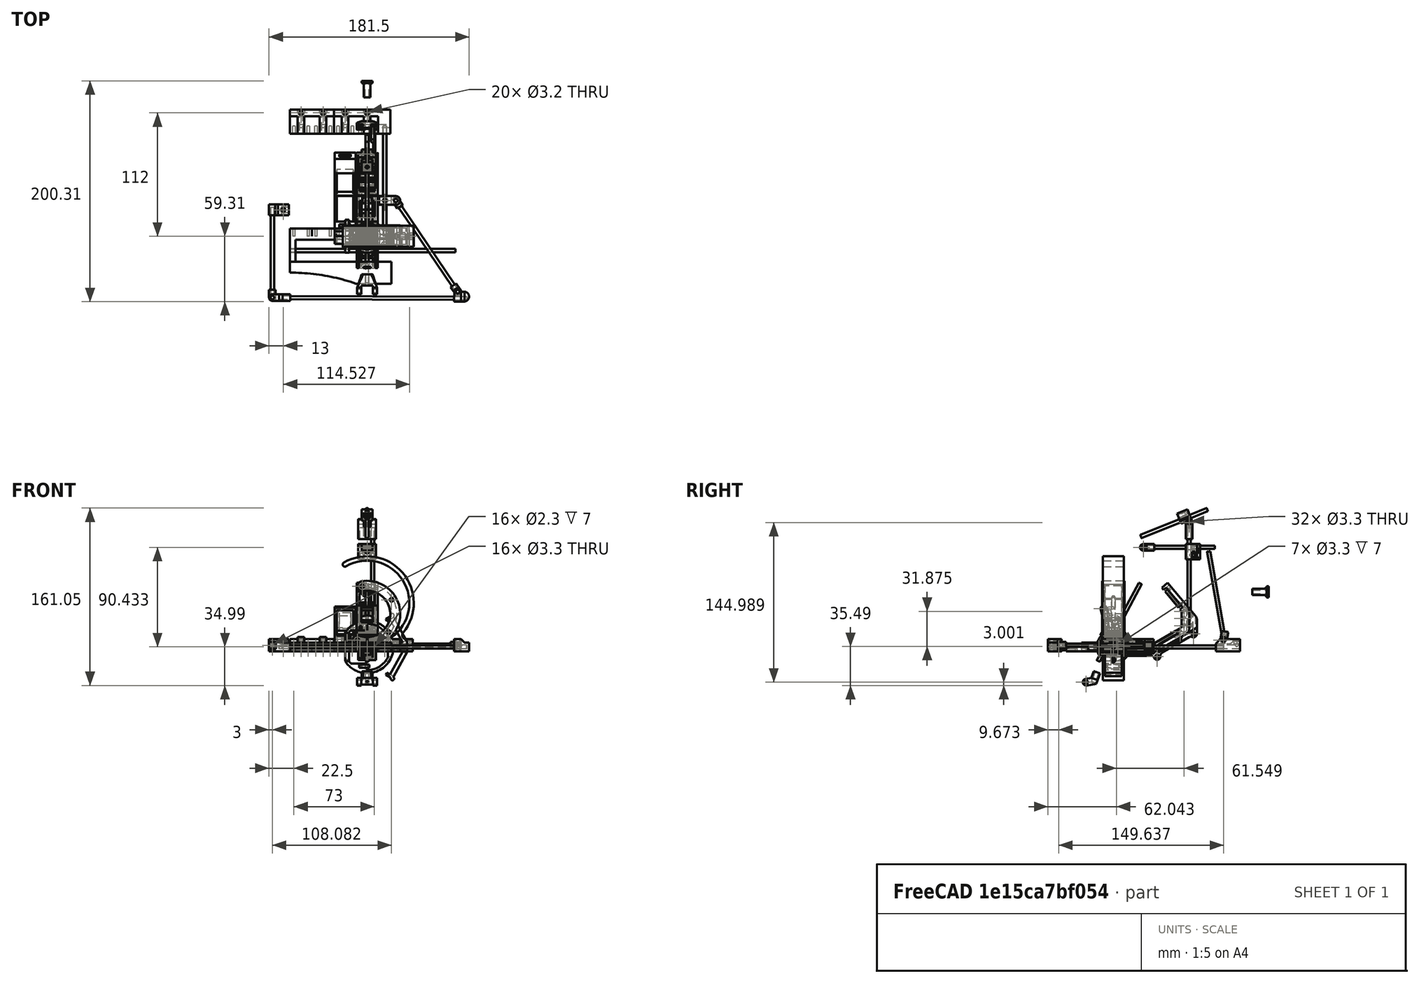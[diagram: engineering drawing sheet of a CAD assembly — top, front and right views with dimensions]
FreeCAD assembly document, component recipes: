
FREECAD ASSEMBLY — COMPONENT RECIPES ("Structure")

This assembly document has 6 components, labeled P0..P5 below (a component is one placed body or linked part). 4 of them carry a construction recipe — the FreeCAD feature program that regenerates the part from scratch, quoted from this document or its linked companion documents; the rest are supplied as boundary geometry only. No exploded tour is included for this assembly.
COMPONENT P0 — recipe-attached ("Base", modeled in this document).
Construction recipe (the document's own serialized feature program — sketch geometry with constraints, then the solid features built on it; lengths are millimeters unless a unit is written):

FEATURE [Sketcher::SketchObject] Sketch263  label="BaseSkeleton_KeyHolder"
  FullyConstrained = false
  MapMode = 5
  Placement = pos=(0,0,0) rot=(0.57735,0.57735,0.57735;2.0944rad)
  Support = -> [YZ_Plane106]
  expr: .Constraints.y0 = <<BaseParameters>>.horizontalRailLength
  expr: .Constraints.z0 = 6 + <<BaseParameters>>.tolerance
  expr: Constraints[13] = Sketch232.Constraints.l1
  expr: Constraints[14] = Sketch232.Constraints.l2
  expr: Constraints[15] = Sketch232.Constraints.l3
  expr: Constraints[16] = Sketch232.Constraints.theta1
  expr: Constraints[17] = Sketch232.Constraints.theta0
  expr: Constraints[27] = Sketch232.Constraints.theta2
  expr: Constraints[36] = <<BaseParameters>>.support0Length
  expr: Constraints[41] = 6 + 2 * <<BaseParameters>>.axisTolerance + <<BaseParameters>>.verticalRailLength
  expr: Constraints[57] = 1.5 + <<BaseParameters>>.axisTolerance
  expr: Constraints[60] = Sketch292.Constraints.y0
  expr: Constraints[69] = Sketch297.Constraints.theta0
  expr: Constraints[70] = Sketch297.Constraints.l0
  expr: Constraints[74] = Sketch203.Constraints.theta0
  expr: Constraints[89] = Sketch284.Constraints.l0 + <<BaseParameters>>.support1Length * 1mm
  sketch-geometry (28):
    g0: LineSegment StartX=0 StartY=0 StartZ=0 EndX=100 EndY=0 EndZ=0
    g1: LineSegment StartX=100 StartY=0 StartZ=0 EndX=100 EndY=6.15 EndZ=0
    g2: LineSegment StartX=100 StartY=6.15 StartZ=0 EndX=102.335 EndY=92.4184 EndZ=0
    g3: LineSegment StartX=100 StartY=6.15 StartZ=0 EndX=100 EndY=26.15 EndZ=0
    g4: LineSegment StartX=26.1808 StartY=28.1109 StartZ=0 EndX=63.4391 EndY=47.1897 EndZ=0
    g5: LineSegment StartX=63.4391 StartY=47.1897 StartZ=0 EndX=81.9391 EndY=81.3515 EndZ=0
    g6: LineSegment StartX=26.1808 StartY=28.1109 StartZ=0 EndX=24.669 EndY=34.9227 EndZ=0
    g7: GeomPoint X=-500 Y=0 Z=0
    g8: LineSegment StartX=24.669 StartY=34.9227 StartZ=0 EndX=24.669 EndY=54.9227 EndZ=0
    g9: LineSegment StartX=24.669 StartY=34.9227 StartZ=0 EndX=14.7136 EndY=52.2688 EndZ=0
    g10: GeomPoint X=46.4566 Y=0 Z=0
    g11: LineSegment StartX=46.4566 StartY=0 StartZ=0 EndX=46.4566 EndY=6 EndZ=0
    g12: LineSegment StartX=26.1808 StartY=28.1109 StartZ=0 EndX=46.4566 EndY=6 EndZ=0
    g13: LineSegment StartX=46.4566 StartY=6 StartZ=0 EndX=46.4566 EndY=26 EndZ=0
    g14: GeomPoint X=100.045 Y=7.7994 Z=0
    g15: GeomPoint X=101.083 Y=46.1708 Z=0
    g16: LineSegment StartX=63.4391 StartY=47.1897 StartZ=0 EndX=150.407 EndY=44.8358 EndZ=0
    g17: LineSegment StartX=63.4391 StartY=47.1897 StartZ=0 EndX=63.4391 EndY=67.1897 EndZ=0
    g18: LineSegment StartX=102.335 StartY=92.4184 StartZ=0 EndX=102.876 EndY=112.411 EndZ=0
    g19: LineSegment StartX=102.335 StartY=92.4184 StartZ=0 EndX=133.365 EndY=146.164 EndZ=0
    g20: LineSegment StartX=102.335 StartY=92.4184 StartZ=0 EndX=97.1388 EndY=95.4184 EndZ=0
    g21: LineSegment StartX=81.9391 StartY=81.3515 StartZ=0 EndX=102.021 EndY=80.808 EndZ=0
    g22: LineSegment StartX=81.9391 StartY=81.3515 StartZ=0 EndX=88.2853 EndY=80.0836 EndZ=0
    g23: LineSegment StartX=88.2853 StartY=80.0836 StartZ=0 EndX=126.04 EndY=145.477 EndZ=0
    g24: LineSegment StartX=81.9391 StartY=81.3515 StartZ=0 EndX=89.0173 EndY=81.3515 EndZ=0
    g25: LineSegment StartX=81.9391 StartY=81.3515 StartZ=0 EndX=82.4803 EndY=101.344 EndZ=0
    g26: LineSegment StartX=81.9391 StartY=81.3515 StartZ=0 EndX=81.9391 EndY=101.352 EndZ=0
    g27: LineSegment StartX=88.2853 StartY=80.0836 StartZ=0 EndX=101.991 EndY=79.7126 EndZ=0
  constraints (96):
    c: Coincident(g0,g-1)
    c: PointOnObject(g0,g-1)
    c: Distance(g0) = 100  'y0'
    c: Coincident(g0,g1)
    c: Vertical(g1)
    c: Distance(g1) = 6.15  'z0'
    c: Coincident(g2,g1)
    c: Coincident(g3,g1)
    c: Vertical(g3)
    c: Distance(g3) = 20
    c: Angle(g2,g3) = 0.0270601  'theta0'
    c: Coincident(g4,g5)
    c: Coincident(g6,g4)
    c: Distance(g6) = 6.97753
    c: Distance(g4) = 41.8591
    c: Distance(g5) = 38.8495
    c: Angle(g5,g4) = 2.54038
    c: Angle(g4,g6) = 1.31593
    c: PointOnObject(g7,g-1)
    c: Distance(g7,g-2) = 500  'yNeg'
    c: DistanceX(g7,g6) = 524.669  'y1'
    c: Distance(g6,g-1) = 34.9227  'z1'
    c: Coincident(g8,g6)
    c: Vertical(g8)
    c: Equal(g8,g3)
    c: Coincident(g9,g6)
    c: Equal(g9,g8)
    c: Angle(g9,g6) = 2.83896
    c: Angle(g8,g9) = 0.521027  'theta1'
    c: PointOnObject(g10,g0)
    c: Distance(g10,g-2) = 46.4566  'y2'
    c: Coincident(g11,g10)
    c: Vertical(g11)
    c: Distance(g11) = 6
    c: Coincident(g12,g4)
    c: Coincident(g12,g11)
    c: Distance(g12) = 30
    c: Coincident(g13,g11)
    c: Vertical(g13)
    c: Equal(g8,g13)
    c: Angle(g13,g12) = 0.742132  'theta2'
    c: Distance(g2) = 86.3
    c: PointOnObject(g14,g2)
    c: Distance(g14,g-1) = 7.7994  'z3'
    c: Distance(g14,g-2) = 100.045  'y3'
    c: PointOnObject(g15,g2)
    c: Distance(g15,g-2) = 101.083  'y4'
    c: Distance(g15,g-1) = 46.1708  'z4'
    c: Coincident(g16,g4)
    c: PointOnObject(g15,g16)
    c: Perpendicular(g16,g2)
    c: Coincident(g17,g4)
    c: Vertical(g17)
    c: Equal(g17,g8)
    c: Distance(g15,g4) = 37.658  'support1y0'
    c: Distance(g2,g-2) = 102.335  'y5'
    c: Distance(g2,g-1) = 92.4184  'z5'
    c: Distance(g14,g1) = 1.65
    c: Parallel(g18,g2)
    c: Distance(g18) = 20
    c: Distance(g20) = 6
    c: Perpendicular(g19,g20)
    c: Coincident(g21,g5)
    c: PointOnObject(g21,g2)
    c: Perpendicular(g2,g21)
    c: Distance(g21) = 20.089  'support2y0'
    c: Distance(g21,g2) = 11.6147  'support2z0'
    c: Coincident(g5,g22)
    c: Coincident(g22,g23)
    c: Angle(g23,g22) = 1.89719
    c: Distance(g22) = 6.47158
    c: PointOnObject(g20,g23)
    c: Coincident(g24,g5)
    c: PointOnObject(g24,g23)
    c: Angle(g23,g24) = 2.0944
    c: Coincident(g25,g5)
    c: Equal(g18,g25)
    c: Parallel(g25,g18)
    c: Coincident(g26,g5)
    c: Vertical(g26)
    c: Perpendicular(g24,g26)
    c: Equal(g25,g26)
    c: Angle(g25,g26) = 0.0270601  'support2theta1'
    c: Perpendicular(g23,g20)
    c: Coincident(g27,g22)
    c: PointOnObject(g27,g2)
    c: Parallel(g27,g21)
    c: Distance(g27) = 13.7108  'support2y1'
    c: Distance(g27,g2) = 12.7105  'support2z1'
    c: Distance(g16) = 87
    c: Angle(g19,g18) = 0.496539  'support2theta0'
    c: Distance(g23) = 75.51
    c: Distance(g19) = 62.06
    c: Coincident(g19,g2)
    c: Coincident(g20,g2)
    c: Coincident(g18,g2)
FEATURE [Sketcher::SketchObject] Sketch264
  FullyConstrained = true
  MapMode = 5
  Placement = pos=(0,0,0) rot=(0.57735,0.57735,0.57735;2.0944rad)
  Support = -> [YZ_Plane107]
  sketch-geometry (4):
    g0: LineSegment StartX=-3 StartY=-4 StartZ=0 EndX=7 EndY=-4 EndZ=0
    g1: LineSegment StartX=7 StartY=-4 StartZ=0 EndX=7 EndY=4 EndZ=0
    g2: LineSegment StartX=7 StartY=4 StartZ=0 EndX=-3 EndY=4 EndZ=0
    g3: LineSegment StartX=-3 StartY=4 StartZ=0 EndX=-3 EndY=-4 EndZ=0
  constraints (11):
    c: Horizontal(g0)
    c: Coincident(g0,g1)
    c: Vertical(g1)
    c: Coincident(g1,g2)
    c: Horizontal(g2)
    c: Coincident(g2,g3)
    c: Coincident(g3,g0)
    c: Distance(g3) = 8
    c: Distance(g0,g-2) = 3
    c: Distance(g0,g-2) = 7  'y0'
    c: Symmetric(g2,g0,g-1)
FEATURE [PartDesign::Pad] Pad169
  Direction = (1,-2e-16,3e-16)
  Length = 20
  Length2 = 10
  Midplane = true
  Placement = pos=(0,0,0) rot=(0.57735,0.57735,0.57735;2.0944rad)
  Profile = -> Sketch264
  ReferenceAxis = -> Sketch264 [N_Axis]
  Type = 0
FEATURE [Sketcher::SketchObject] Sketch265
  FullyConstrained = true
  MapMode = 5
  Placement = pos=(0,0,0) rot=(1,0,0;1.5708rad)
  Support = -> [XZ_Plane107]
  expr: Constraints[2] = 2 + <<BaseParameters>>.axisTolerance * 2
  expr: Constraints[6] = 3 + <<BaseParameters>>.axisTolerance * 2
  sketch-geometry (3):
    g0: Circle CenterX=-6.5 CenterY=0 CenterZ=0 NormalX=0 NormalY=0 NormalZ=1 AngleXU=0 Radius=1.15
    g1: Circle CenterX=6.5 CenterY=0 CenterZ=0 NormalX=0 NormalY=0 NormalZ=1 AngleXU=0 Radius=1.15
    g2: Circle CenterX=0 CenterY=0 CenterZ=0 NormalX=0 NormalY=0 NormalZ=1 AngleXU=0 Radius=1.65
  constraints (7):
    c: PointOnObject(g0,g-1)
    c: Equal(g0,g1)
    c: Diameter(g1) = 2.3
    c: Distance(g0,g1) = 13
    c: Symmetric(g0,g1,g-2)
    c: Coincident(g2,g-1)
    c: Diameter(g2) = 3.3
FEATURE [PartDesign::Pocket] Pocket085
  BaseFeature = -> Pad169
  Direction = (0,1,2e-16)
  Length = 7
  Length2 = 5
  Placement = pos=(0,0,0) rot=(0.57735,0.57735,0.57735;2.0944rad)
  Profile = -> Sketch265
  ReferenceAxis = -> Sketch265 [N_Axis]
  Type = 0
FEATURE [PartDesign::Body] Body065  label="BaseStructure0"
  Group = -> [Sketch264,Pad169,Sketch265,Pocket085]
  Origin = -> Origin107
  Tip = -> Pocket085
FEATURE [Sketcher::SketchObject] Sketch266
  FullyConstrained = true
  MapMode = 5
  Placement = pos=(0,0,0) rot=(0.57735,0.57735,0.57735;2.0944rad)
  Support = -> [YZ_Plane109]
  expr: Constraints[13] = 3 + <<BaseParameters>>.tolerance
  expr: Constraints[15] = 3 + 2 * <<BaseParameters>>.axisTolerance
  sketch-geometry (6):
    g0: LineSegment StartX=-7 StartY=3 StartZ=0 EndX=-7 EndY=-4 EndZ=0
    g1: LineSegment StartX=-7 StartY=-4 StartZ=0 EndX=3 EndY=-4 EndZ=0
    g2: LineSegment StartX=3 StartY=-4 StartZ=0 EndX=3 EndY=6.15 EndZ=0
    g3: ArcOfCircle CenterX=0 CenterY=6.15 CenterZ=0 NormalX=0 NormalY=0 NormalZ=1 AngleXU=0 Radius=3 StartAngle=0 EndAngle=2.39518
    g4: LineSegment StartX=-2.20238 StartY=8.18704 StartZ=0 EndX=-7 EndY=3 EndZ=0
    g5: Circle CenterX=0 CenterY=6.15 CenterZ=0 NormalX=0 NormalY=0 NormalZ=1 AngleXU=0 Radius=1.65
  constraints (16):
    c: Vertical(g0)
    c: Coincident(g0,g1)
    c: Horizontal(g1)
    c: Coincident(g1,g2)
    c: Vertical(g2)
    c: Tangent(g2,g3) = -1.5708
    c: Tangent(g3,g4) = -1.5708
    c: Coincident(g4,g0)
    c: Distance(g0) = 7
    c: Distance(g0,g-1) = 4
    c: Distance(g1,g-2) = 3
    c: Distance(g0,g-2) = 7
    c: PointOnObject(g3,g-2)
    c: DistanceY(g0,g3) = 3.15
    c: Coincident(g5,g3)
    c: Diameter(g5) = 3.3
FEATURE [PartDesign::Pad] Pad170
  Direction = (1,-2e-16,3e-16)
  Length = 20
  Length2 = 10
  Midplane = true
  Placement = pos=(0,0,0) rot=(0.57735,0.57735,0.57735;2.0944rad)
  Profile = -> Sketch266
  ReferenceAxis = -> Sketch266 [N_Axis]
  Type = 0
FEATURE [Sketcher::SketchObject] Sketch268
  FullyConstrained = true
  MapMode = 5
  Placement = pos=(0,0,0) rot=(1,0,0;1.5708rad)
  Support = -> [XZ_Plane110]
  sketch-geometry (1):
    g0: Circle CenterX=0 CenterY=0 CenterZ=0 NormalX=0 NormalY=0 NormalZ=1 AngleXU=0 Radius=1
  constraints (2):
    c: Coincident(g0,g-1)
    c: Diameter(g0) = 2
FEATURE [PartDesign::Pad] Pad171
  Direction = (0,-1,-2e-16)
  Length = 100
  Length2 = 10
  Placement = pos=(0,0,0) rot=(1,0,0;1.5708rad)
  Profile = -> Sketch268
  ReferenceAxis = -> Sketch268 [N_Axis]
  Reversed = true
  Type = 0
  expr: Length = <<BaseParameters>>.horizontalRailLength
FEATURE [PartDesign::Body] Body067  label="HorizontalRail"
  Group = -> [Sketch268,Pad171]
  Origin = -> Origin110
  Placement = pos=(6.5,0,0) rot=(0,0,1;0rad)
  Tip = -> Pad171
FEATURE [Sketcher::SketchObject] Sketch269
  FullyConstrained = true
  MapMode = 5
  Placement = pos=(0,0,0) rot=(1,0,0;1.5708rad)
  Support = -> [XZ_Plane109]
  expr: Constraints[3] = 2 + <<BaseParameters>>.axisTolerance * 2
  expr: Constraints[6] = 3 + 2 * <<BaseParameters>>.axisTolerance
  sketch-geometry (3):
    g0: Circle CenterX=-6.5 CenterY=0 CenterZ=0 NormalX=0 NormalY=0 NormalZ=1 AngleXU=0 Radius=1.15
    g1: Circle CenterX=6.5 CenterY=0 CenterZ=0 NormalX=0 NormalY=0 NormalZ=1 AngleXU=0 Radius=1.15
    g2: Circle CenterX=0 CenterY=0 CenterZ=0 NormalX=0 NormalY=0 NormalZ=1 AngleXU=0 Radius=1.65
  constraints (7):
    c: PointOnObject(g0,g-1)
    c: Symmetric(g0,g1,g-2)
    c: Equal(g0,g1)
    c: Diameter(g1) = 2.3
    c: Distance(g1,g0) = 13
    c: Coincident(g2,g-1)
    c: Diameter(g2) = 3.3
FEATURE [PartDesign::Pocket] Pocket087
  BaseFeature = -> Pad170
  Direction = (0,1,2e-16)
  Length = 7
  Length2 = 5
  Placement = pos=(0,0,0) rot=(0.57735,0.57735,0.57735;2.0944rad)
  Profile = -> Sketch269
  ReferenceAxis = -> Sketch269 [N_Axis]
  Reversed = true
  Type = 0
FEATURE [Sketcher::SketchObject] Sketch278
  FullyConstrained = true
  MapMode = 5
  Support = -> [XY_Plane114]
  sketch-geometry (1):
    g0: Circle CenterX=0 CenterY=0 CenterZ=0 NormalX=0 NormalY=0 NormalZ=1 AngleXU=0 Radius=1.5
  constraints (2):
    c: Coincident(g0,g-1)
    c: Diameter(g0) = 3
FEATURE [PartDesign::Pad] Pad175
  Direction = (0,0,1)
  Length = 80
  Length2 = 10
  Profile = -> Sketch278
  ReferenceAxis = -> Sketch278 [N_Axis]
  Type = 0
  expr: Length = <<BaseParameters>>.verticalRailLength
FEATURE [PartDesign::Body] Body070  label="VerticalRail"
  Group = -> [Sketch278,Pad175]
  Origin = -> Origin114
  Placement = pos=(5,100.285,7.77526) rot=(1,0,0;0.17338rad)
  Tip = -> Pad175
  expr: .Placement.Base.y = Sketch403.Constraints.y4
  expr: .Placement.Base.z = <<BaseSkeleton_KeyHolder001>>.Constraints.z4
  expr: .Placement.Rotation.Angle = 180deg - <<BaseSkeleton_KeyHolder001>>.Constraints.theta1
FEATURE [Sketcher::SketchObject] Sketch301  label="BaseSkeleton_Joystick"
  FullyConstrained = false
  MapMode = 5
  Support = -> [XY_Plane106]
  expr: Constraints[13] = Sketch313.Constraints.x0
  expr: Constraints[21] = 1.5 + <<BaseParameters>>.axisTolerance + <<BaseParameters>>.joystickBaseArm0Length
  expr: Constraints[23] = 1.5 + <<BaseParameters>>.axisTolerance
  expr: Constraints[26] = 1.5 + <<BaseParameters>>.axisTolerance
  expr: Constraints[31] = Sketch321.Constraints.y0
  expr: Constraints[38] = <<BaseParameters>>.joystickBaseArm2Length
  expr: Constraints[46] = 6 + <<BaseParameters>>.tolerance
  expr: Constraints[48] = <<BaseParameters>>.horizontalRailLength
  expr: Constraints[54] = <<BaseParameters>>.joystickBaseArm1Length
  expr: Constraints[55] = 1.5 + <<BaseParameters>>.axisTolerance
  sketch-geometry (21):
    g0: LineSegment StartX=-76 StartY=100 StartZ=0 EndX=-76 EndY=0 EndZ=0
    g1: LineSegment StartX=-76 StartY=25.9821 StartZ=0 EndX=-86 EndY=25.9821 EndZ=0
    g2: LineSegment StartX=-79.85 StartY=-55.6906 StartZ=0 EndX=90.1488 EndY=-56.3178 EndZ=0
    g3: LineSegment StartX=83.0978 StartY=-51.6534 StartZ=0 EndX=26 EndY=32.4451 EndZ=0
    g4: LineSegment StartX=26 StartY=32.4451 StartZ=0 EndX=16 EndY=32.4451 EndZ=0
    g5: LineSegment StartX=16 StartY=0 StartZ=0 EndX=16 EndY=100 EndZ=0
    g6: LineSegment StartX=26 StartY=32.4451 StartZ=0 EndX=26 EndY=42.4451 EndZ=0
    g7: GeomPoint X=26.9268 Y=31.08 Z=0
    g8: LineSegment StartX=83.0978 StartY=-51.6534 StartZ=0 EndX=82.171 EndY=-50.2883 EndZ=0
    g9: LineSegment StartX=82.171 StartY=-50.2883 StartZ=0 EndX=82.1489 EndY=-56.2883 EndZ=0
    g10: LineSegment StartX=82.1489 StartY=-56.2883 StartZ=0 EndX=82.1489 EndY=-46.2883 EndZ=0
    g11: LineSegment StartX=90.1488 StartY=-56.3178 StartZ=0 EndX=100.149 EndY=-56.3178 EndZ=0
    g12: LineSegment StartX=-86 StartY=-55.6679 StartZ=0 EndX=-79.85 EndY=-55.6906 EndZ=0
    g13: LineSegment StartX=-86 StartY=25.9821 StartZ=0 EndX=-86 EndY=-54.0179 EndZ=0
    g14: LineSegment StartX=-86 StartY=-54.0179 StartZ=0 EndX=-86 EndY=-55.6679 EndZ=0
    g15: GeomPoint X=-200 Y=0 Z=0
    g16: GeomPoint X=-15.423 Y=-55.9283 Z=0
    g17: LineSegment StartX=-15.423 StartY=-55.9283 StartZ=0 EndX=0.701986 EndY=-47.8962 EndZ=0
    g18: LineSegment StartX=-15.423 StartY=-55.9283 StartZ=0 EndX=-15.423 EndY=-45.9283 EndZ=0
    g19: LineSegment StartX=-15.423 StartY=-55.9283 StartZ=0 EndX=-6.472 EndY=-51.4697 EndZ=0
    g20: GeomPoint X=40.8322 Y=-56.1358 Z=0
  constraints (77):
    c: Vertical(g0)
    c: Distance(g-1,g0) = 76
    c: PointOnObject(g1,g0)
    c: Horizontal(g1)
    c: Coincident(g1,g13)
    c: Coincident(g12,g2)
    c: Coincident(g3,g4)
    c: Horizontal(g4)
    c: PointOnObject(g5,g-1)
    c: Vertical(g5)
    c: PointOnObject(g0,g-1)
    c: Horizontal(g0,g5)
    c: Distance(g5,g-2) = 16
    c: Distance(g4) = 10
    c: Distance(g1) = 10
    c: PointOnObject(g4,g5)
    c: Distance(g4,g-1) = 32.4451  'y0'
    c: Coincident(g6,g3)
    c: Vertical(g6)
    c: Angle(g3,g6) = 2.54514  'theta0'
    c: Distance(g6) = 10
    c: Distance(g3) = 101.65
    c: PointOnObject(g7,g3)
    c: Distance(g7,g3) = 1.65
    c: Distance(g7,g-2) = 26.9268  'x2'
    c: Distance(g7,g-1) = 31.08  'y2'
    c: Distance(g8) = 1.65
    c: Distance(g8,g-2) = 82.171  'x1'
    c: Distance(g8,g-1) = 50.2883  'y1'
    c: PointOnObject(g9,g2)
    c: Perpendicular(g2,g9)
    c: Distance(g9) = 6
    c: Distance(g2,g9) = 8
    c: Coincident(g10,g9)
    c: Vertical(g10)
    c: Equal(g10,g6)
    c: Distance(g2,g-1) = 56.3178  'y3'
    c: Distance(g2,g-2) = 90.1488  'x3'
    c: Distance(g2) = 170
    c: Coincident(g11,g2)
    c: Horizontal(g11)
    c: Distance(g11) = 10
    c: Angle(g11,g2) = 3.1379  'theta1'
    c: Distance(g12,g-2) = 79.85  'x4'
    c: Distance(g12,g-1) = 55.6906  'y4'
    c: Coincident(g14,g12)
    c: Distance(g12) = 6.15
    c: Parallel(g12,g2)
    c: Distance(g5) = 100
    c: Distance(g14,g-2) = 86  'x5'
    c: Distance(g14,g-1) = 55.6679  'y5'
    c: Coincident(g13,g14)
    c: Vertical(g13)
    c: Vertical(g14)
    c: Distance(g13) = 80
    c: Distance(g14) = 1.65
    c: Distance(g1,g-1) = 25.9821  'y6'
    c: Distance(g1,g-2) = 76  'x6'
    c: Coincident(g8,g3)
    c: Parallel(g8,g3)
    c: Coincident(g8,g9)
    c: PointOnObject(g15,g-1)
    c: Distance(g15,g-2) = 200  'xNeg'
    c: PointOnObject(g16,g2)
    c: DistanceX(g15,g16) = 184.577  'x7n'
    c: Distance(g16,g-1) = 55.9283  'y7'
    c: Coincident(g17,g16)
    c: Coincident(g18,g16)
    c: Vertical(g18)
    c: Equal(g18,g10)
    c: Coincident(g19,g16)
    c: Equal(g18,g19)
    c: Angle(g19,g18) = 1.10866  'theta7'
    c: Parallel(g19,g17)
    c: PointOnObject(g20,g2)
    c: Distance(g20,g-2) = 40.8322  'x8'
    c: Distance(g20,g-1) = 56.1358  'y8'
FEATURE [Sketcher::SketchObject] Sketch306
  AttachmentOffset = pos=(0,0,5) rot=(0,0,1;0rad)
  FullyConstrained = true
  MapMode = 5
  Placement = pos=(5,-1.1e-15,1.1e-15) rot=(0.57735,0.57735,0.57735;2.0944rad)
  Support = -> [YZ_Plane127]
  sketch-geometry (4):
    g0: LineSegment StartX=3 StartY=3 StartZ=0 EndX=-7 EndY=3 EndZ=0
    g1: LineSegment StartX=-7 StartY=3 StartZ=0 EndX=-7 EndY=-4 EndZ=0
    g2: LineSegment StartX=-7 StartY=-4 StartZ=0 EndX=3 EndY=-4 EndZ=0
    g3: LineSegment StartX=3 StartY=-4 StartZ=0 EndX=3 EndY=3 EndZ=0
  constraints (12):
    c: Coincident(g0,g1)
    c: Coincident(g1,g2)
    c: Coincident(g2,g3)
    c: Coincident(g3,g0)
    c: Horizontal(g0)
    c: Horizontal(g2)
    c: Vertical(g1)
    c: Vertical(g3)
    c: Distance(g0,g-1) = 3
    c: Distance(g0,g-2) = 3
    c: Distance(g2,g-1) = 4
    c: Distance(g0,g-2) = 7
FEATURE [PartDesign::Pad] Pad189
  Direction = (1,-2e-16,3e-16)
  Length = 11
  Length2 = 10
  Placement = pos=(0,0,0) rot=(0.57735,0.57735,0.57735;2.0944rad)
  Profile = -> Sketch306
  ReferenceAxis = -> Sketch306 [N_Axis]
  Reversed = true
  Type = 0
FEATURE [Sketcher::SketchObject] Sketch307
  FullyConstrained = true
  MapMode = 5
  Placement = pos=(0,0,0) rot=(1,0,0;1.5708rad)
  Support = -> [XZ_Plane127]
  expr: Constraints[1] = 3 + 2 * <<BaseParameters>>.axisTolerance
  sketch-geometry (1):
    g0: Circle CenterX=0 CenterY=0 CenterZ=0 NormalX=0 NormalY=0 NormalZ=1 AngleXU=0 Radius=1.65
  constraints (2):
    c: Coincident(g0,g-1)
    c: Diameter(g0) = 3.3
FEATURE [PartDesign::Pocket] Pocket106
  BaseFeature = -> Pad189
  Direction = (0,1,2e-16)
  Length = 7
  Length2 = 5
  Placement = pos=(0,0,0) rot=(0.57735,0.57735,0.57735;2.0944rad)
  Profile = -> Sketch307
  ReferenceAxis = -> Sketch307 [N_Axis]
  Reversed = true
  Type = 0
FEATURE [Sketcher::SketchObject] Sketch309
  FullyConstrained = true
  MapMode = 5
  Placement = pos=(0,0,0) rot=(1,0,0;1.5708rad)
  Support = -> [XZ_Plane129]
  sketch-geometry (1):
    g0: Circle CenterX=0 CenterY=0 CenterZ=0 NormalX=0 NormalY=0 NormalZ=1 AngleXU=0 Radius=1.5
  constraints (2):
    c: Coincident(g0,g-1)
    c: Diameter(g0) = 3
FEATURE [PartDesign::Pad] Pad191
  Direction = (0,-1,-2e-16)
  Length = 100
  Length2 = 10
  Placement = pos=(0,0,0) rot=(1,0,0;1.5708rad)
  Profile = -> Sketch309
  ReferenceAxis = -> Sketch309 [N_Axis]
  Reversed = true
  Type = 0
  expr: Length = <<BaseParameters>>.horizontalRailLength
FEATURE [PartDesign::Body] Body083  label="OLEDRail"
  Group = -> [Sketch309,Pad191]
  Origin = -> Origin129
  Placement = pos=(16,0,0) rot=(0,0,1;0rad)
  Tip = -> Pad191
FEATURE [Sketcher::SketchObject] Sketch313
  AttachmentOffset = pos=(0,0,-4) rot=(0,0,1;0rad)
  FullyConstrained = true
  MapMode = 5
  Placement = pos=(0,0,-4) rot=(0,0,1;0rad)
  Support = -> [XY_Plane131]
  expr: Constraints[12] = 3 + <<BaseParameters>>.axisTolerance * 2
  sketch-geometry (5):
    g0: LineSegment StartX=-5 StartY=4 StartZ=0 EndX=10 EndY=4 EndZ=0
    g1: LineSegment StartX=10 StartY=-4 StartZ=0 EndX=-5 EndY=-4 EndZ=0
    g2: LineSegment StartX=-5 StartY=-4 StartZ=0 EndX=-5 EndY=4 EndZ=0
    g3: ArcOfCircle CenterX=10 CenterY=0 CenterZ=0 NormalX=0 NormalY=0 NormalZ=1 AngleXU=0 Radius=4 StartAngle=4.71239 EndAngle=7.85398
    g4: Circle CenterX=10 CenterY=0 CenterZ=0 NormalX=0 NormalY=0 NormalZ=1 AngleXU=0 Radius=1.65
  constraints (13):
    c: Coincident(g1,g2)
    c: Coincident(g2,g0)
    c: Horizontal(g0)
    c: Horizontal(g1)
    c: Vertical(g2)
    c: Distance(g2) = 8
    c: Distance(g0,g-2) = 5
    c: PointOnObject(g3,g-1)
    c: Tangent(g3,g0) = 1.5708
    c: Tangent(g3,g1) = 1.5708
    c: Distance(g0,g-2) = 10  'x0'
    c: Coincident(g4,g3)
    c: Diameter(g4) = 3.3
FEATURE [PartDesign::Pad] Pad194
  Direction = (0,0,1)
  Length = 11
  Length2 = 10
  Profile = -> Sketch313
  ReferenceAxis = -> Sketch313 [N_Axis]
  Type = 0
FEATURE [Sketcher::SketchObject] Sketch314
  FullyConstrained = true
  MapMode = 5
  Placement = pos=(0,0,0) rot=(1,0,0;1.5708rad)
  Support = -> [XZ_Plane131]
  expr: Constraints[1] = 3 + 2 * <<BaseParameters>>.axisTolerance
  sketch-geometry (1):
    g0: Circle CenterX=0 CenterY=0 CenterZ=0 NormalX=0 NormalY=0 NormalZ=1 AngleXU=0 Radius=1.65
  constraints (2):
    c: Coincident(g0,g-1)
    c: Diameter(g0) = 3.3
FEATURE [PartDesign::Pocket] Pocket108
  BaseFeature = -> Pad194
  Direction = (0,1,2e-16)
  Length = 10
  Length2 = 5
  Midplane = true
  Profile = -> Sketch314
  ReferenceAxis = -> Sketch314 [N_Axis]
  Type = 0
FEATURE [Sketcher::SketchObject] Sketch315
  AttachmentOffset = pos=(0,0,4) rot=(0,0,1;0rad)
  FullyConstrained = true
  MapMode = 5
  Placement = pos=(0,0,4) rot=(0,0,1;0rad)
  Support = -> [XY_Plane131]
  sketch-geometry (10):
    g0: LineSegment StartX=3.23316 StartY=0 StartZ=0 EndX=1.61658 EndY=2.8 EndZ=0
    g1: LineSegment StartX=1.61658 StartY=2.8 StartZ=0 EndX=-1.61658 EndY=2.8 EndZ=0
    g2: LineSegment StartX=-1.61658 StartY=2.8 StartZ=0 EndX=-3.23316 EndY=-2.0415e-12 EndZ=0
    g3: LineSegment StartX=-3.23316 StartY=-2.0415e-12 StartZ=0 EndX=-1.61658 EndY=-2.8 EndZ=0
    g4: LineSegment StartX=-1.61658 StartY=-2.8 StartZ=0 EndX=1.61658 EndY=-2.8 EndZ=0
    g5: LineSegment StartX=1.61658 StartY=-2.8 StartZ=0 EndX=3.23316 EndY=0 EndZ=0
    g6: Circle CenterX=0 CenterY=0 CenterZ=0 NormalX=0 NormalY=0 NormalZ=1 AngleXU=0 Radius=3.23316
    g7: LineSegment StartX=-1.61658 StartY=2.8 StartZ=0 EndX=-5.61658 EndY=2.8 EndZ=0
    g8: LineSegment StartX=-5.61658 StartY=2.8 StartZ=0 EndX=-5.61658 EndY=-2.8 EndZ=0
    g9: LineSegment StartX=-5.61658 StartY=-2.8 StartZ=0 EndX=-1.61658 EndY=-2.8 EndZ=0
  constraints (24):
    c: Coincident(g0,g1)
    c: Coincident(g1,g2)
    c: Coincident(g2,g3)
    c: Coincident(g3,g4)
    c: Coincident(g4,g5)
    c: Coincident(g5,g0)
    c: Equal(g0, g1-g5) x5
    c: PointOnObject(g0,g6)
    c: PointOnObject(g1,g6)
    c: PointOnObject(g2,g6)
    c: PointOnObject(g3,g6)
    c: PointOnObject(g4,g6)
    c: PointOnObject(g5,g6)
    c: PointOnObject(g5,g-1)
    c: Distance(g0,g4) = 5.6
    c: Coincident(g6,g-1)
    c: Coincident(g1,g7)
    c: Horizontal(g7)
    c: Coincident(g7,g8)
    c: Vertical(g8)
    c: Coincident(g8,g9)
    c: Coincident(g9,g3)
    c: Horizontal(g9)
    c: Distance(g7) = 4
FEATURE [PartDesign::Pocket] Pocket109
  BaseFeature = -> Pocket108
  Direction = (0,0,-1)
  Length = 2.6
  Length2 = 5
  Midplane = true
  Profile = -> Sketch315
  ReferenceAxis = -> Sketch315 [N_Axis]
  Type = 0
FEATURE [Sketcher::SketchObject] Sketch316
  FullyConstrained = true
  MapMode = 5
  Support = -> [XY_Plane131]
  expr: Constraints[1] = 3 + 2 * <<BaseParameters>>.screwHoleTolerance
  sketch-geometry (1):
    g0: Circle CenterX=0 CenterY=0 CenterZ=0 NormalX=0 NormalY=0 NormalZ=1 AngleXU=0 Radius=1.6
  constraints (2):
    c: Coincident(g0,g-1)
    c: Diameter(g0) = 3.2
FEATURE [PartDesign::Pocket] Pocket110
  BaseFeature = -> Pocket109
  Direction = (0,0,-1)
  Length = 9
  Length2 = 5
  Profile = -> Sketch316
  ReferenceAxis = -> Sketch316 [N_Axis]
  Reversed = true
  Type = 0
FEATURE [Sketcher::SketchObject] Sketch317
  FullyConstrained = true
  MapMode = 5
  Placement = pos=(0,0,0) rot=(1,0,0;1.5708rad)
  Support = -> [XZ_Plane131]
  expr: .Constraints.z0 = <<BaseParameters>>.joystickArmZoffset
  expr: Constraints[10] = 6 + 2 * <<BaseParameters>>.tolerance
  expr: Constraints[8] = Sketch313.Constraints.x0
  sketch-geometry (7):
    g0: LineSegment StartX=14 StartY=4.65 StartZ=0 EndX=6 EndY=4.65 EndZ=0
    g1: LineSegment StartX=6 StartY=4.65 StartZ=0 EndX=6 EndY=-1.65 EndZ=0
    g2: LineSegment StartX=6 StartY=-1.65 StartZ=0 EndX=14 EndY=-1.65 EndZ=0
    g3: LineSegment StartX=14 StartY=-1.65 StartZ=0 EndX=14 EndY=4.65 EndZ=0
    g4: GeomPoint X=10 Y=4.65 Z=0
    g5: GeomPoint X=6 Y=1.5 Z=0
    g6: LineSegment StartX=6 StartY=1.5 StartZ=0 EndX=0 EndY=1.5 EndZ=0
  constraints (17):
    c: Coincident(g0,g1)
    c: Coincident(g1,g2)
    c: Coincident(g2,g3)
    c: Coincident(g3,g0)
    c: Horizontal(g0)
    c: Horizontal(g2)
    c: Vertical(g1)
    c: Distance(g2,g-2) = 14
    c: Distance(g4,g-2) = 10
    c: Symmetric(g0,g0,g4)
    c: Distance(g3) = 6.3
    c: Vertical(g3)
    c: Symmetric(g0,g1,g5)
    c: Coincident(g6,g5)
    c: PointOnObject(g6,g-2)
    c: Distance(g6,g-1) = 1.5  'z0'
    c: Horizontal(g6)
FEATURE [PartDesign::Pocket] Pocket111
  BaseFeature = -> Pocket110
  Direction = (0,1,2e-16)
  Length = 10
  Length2 = 5
  Midplane = true
  Profile = -> Sketch317
  ReferenceAxis = -> Sketch317 [N_Axis]
  Type = 0
FEATURE [PartDesign::Body] Body085  label="JoystickBaseSlider0"
  Group = -> [Sketch313,Pad194,Sketch314,Pocket108,Sketch315,Pocket109,Sketch316,Pocket110,Sketch317,Pocket111]
  Origin = -> Origin131
  Placement = pos=(16,32.4451,0) rot=(0,0,1;0rad)
  Tip = -> Pocket111
  expr: .Placement.Base.y = Sketch301.Constraints.y0
FEATURE [Sketcher::SketchObject] Sketch318
  FullyConstrained = true
  MapMode = 5
  Support = -> [XY_Plane132]
  expr: Constraints[13] = 3 + 2 * <<BaseParameters>>.axisTolerance
  sketch-geometry (5):
    g0: LineSegment StartX=-3 StartY=4e-16 StartZ=0 EndX=-3 EndY=7 EndZ=0
    g1: LineSegment StartX=-3 StartY=7 StartZ=0 EndX=3 EndY=7 EndZ=0
    g2: LineSegment StartX=3 StartY=7 StartZ=0 EndX=3 EndY=-9e-16 EndZ=0
    g3: ArcOfCircle CenterX=0 CenterY=0 CenterZ=0 NormalX=0 NormalY=0 NormalZ=1 AngleXU=0 Radius=3 StartAngle=3.14159 EndAngle=6.28319
    g4: Circle CenterX=0 CenterY=0 CenterZ=0 NormalX=0 NormalY=0 NormalZ=1 AngleXU=0 Radius=1.65
  constraints (14):
    c: PointOnObject(g0,g-1)
    c: Vertical(g0)
    c: Coincident(g0,g1)
    c: Horizontal(g1)
    c: Coincident(g1,g2)
    c: PointOnObject(g2,g-1)
    c: Vertical(g2)
    c: Coincident(g3,g-1)
    c: Coincident(g3,g0)
    c: Coincident(g3,g2)
    c: Distance(g1) = 6
    c: Distance(g2) = 7
    c: Coincident(g4,g3)
    c: Diameter(g4) = 3.3
FEATURE [PartDesign::Pad] Pad195
  Direction = (0,0,1)
  Length = 6
  Length2 = 10
  Midplane = true
  Profile = -> Sketch318
  ReferenceAxis = -> Sketch318 [N_Axis]
  Type = 0
FEATURE [Sketcher::SketchObject] Sketch319
  FullyConstrained = true
  MapMode = 5
  Placement = pos=(0,0,0) rot=(1,0,0;1.5708rad)
  Support = -> [XZ_Plane132]
  expr: Constraints[1] = 3 + 2 * <<BaseParameters>>.axisTolerance
  sketch-geometry (1):
    g0: Circle CenterX=0 CenterY=0 CenterZ=0 NormalX=0 NormalY=0 NormalZ=1 AngleXU=0 Radius=1.65
  constraints (2):
    c: Coincident(g0,g-1)
    c: Diameter(g0) = 3.3
FEATURE [PartDesign::Pocket] Pocket112
  BaseFeature = -> Pad195
  Direction = (0,1,2e-16)
  Length = 8
  Length2 = 5
  Profile = -> Sketch319
  ReferenceAxis = -> Sketch319 [N_Axis]
  Type = 0
FEATURE [PartDesign::Body] Body086  label="JoystickBaseHinge0"
  Group = -> [Sketch318,Pad195,Sketch319,Pocket112]
  Origin = -> Origin132
  Placement = pos=(26,32.4451,1.5) rot=(0,0,1;3.73804rad)
  Tip = -> Pocket112
  expr: .Placement.Base.x = 16mm + Sketch313.Constraints.x0
  expr: .Placement.Base.y = Sketch301.Constraints.y0
  expr: .Placement.Base.z = Sketch317.Constraints.z0
  expr: .Placement.Rotation.Angle = -Sketch301.Constraints.theta0
FEATURE [Sketcher::SketchObject] Sketch320
  FullyConstrained = true
  MapMode = 5
  Placement = pos=(0,0,0) rot=(1,0,0;1.5708rad)
  Support = -> [XZ_Plane133]
  sketch-geometry (1):
    g0: Circle CenterX=0 CenterY=0 CenterZ=0 NormalX=0 NormalY=0 NormalZ=1 AngleXU=0 Radius=1.5
  constraints (2):
    c: Coincident(g0,g-1)
    c: Diameter(g0) = 3
FEATURE [PartDesign::Pad] Pad196
  Direction = (0,-1,-2e-16)
  Length = 100
  Length2 = 10
  Placement = pos=(0,0,0) rot=(1,0,0;1.5708rad)
  Profile = -> Sketch320
  ReferenceAxis = -> Sketch320 [N_Axis]
  Reversed = true
  Type = 0
  expr: Length = <<BaseParameters>>.joystickBaseArm0Length
FEATURE [PartDesign::Body] Body087  label="JoystickBaseArm0"
  Group = -> [Sketch320,Pad196]
  Origin = -> Origin133
  Placement = pos=(26.9268,31.08,1.5) rot=(0,0,1;3.73804rad)
  Tip = -> Pad196
  expr: .Placement.Base.x = Sketch301.Constraints.x2
  expr: .Placement.Base.y = Sketch301.Constraints.y2
  expr: .Placement.Base.z = Sketch317.Constraints.z0
  expr: .Placement.Rotation.Angle = -Sketch301.Constraints.theta0
FEATURE [PartDesign::Pocket] Pocket113
  BaseFeature = -> Pad195
  Direction = (0,1,2e-16)
  Length = 8
  Length2 = 5
  Profile = -> Sketch319
  ReferenceAxis = -> Sketch319 [N_Axis]
  Type = 0
FEATURE [PartDesign::Body] Body089  label="JoystickBaseHinge1"
  Group = -> [Pocket113]
  Origin = -> Origin135
  Placement = pos=(82.171,-50.2883,1.5) rot=(0,0,1;0.596451rad)
  Tip = -> Pocket113
  expr: .Placement.Base.x = Sketch301.Constraints.x1
  expr: .Placement.Base.y = -Sketch301.Constraints.y1
  expr: .Placement.Base.z = Sketch317.Constraints.z0
  expr: .Placement.Rotation.Angle = 180deg - Sketch301.Constraints.theta0
FEATURE [Sketcher::SketchObject] Sketch321
  AttachmentOffset = pos=(0,0,-4) rot=(0,0,1;0rad)
  FullyConstrained = true
  MapMode = 5
  Placement = pos=(0,0,-4) rot=(0,0,1;0rad)
  Support = -> [XY_Plane136]
  expr: Constraints[10] = 3 + <<BaseParameters>>.tolerance
  expr: Constraints[14] = 3 + 2 * <<BaseParameters>>.axisTolerance
  sketch-geometry (7):
    g0: ArcOfCircle CenterX=0 CenterY=0 CenterZ=0 NormalX=0 NormalY=0 NormalZ=1 AngleXU=0 Radius=3.15 StartAngle=0 EndAngle=3.14159
    g1: LineSegment StartX=-3.15 StartY=4e-16 StartZ=0 EndX=-3.15 EndY=-9 EndZ=0
    g2: LineSegment StartX=-3.15 StartY=-9 StartZ=0 EndX=5.85 EndY=-9 EndZ=0
    g3: LineSegment StartX=5.85 StartY=0 StartZ=0 EndX=3.15 EndY=0 EndZ=0
    g4: ArcOfCircle CenterX=5.85 CenterY=-4.5 CenterZ=0 NormalX=0 NormalY=0 NormalZ=1 AngleXU=0 Radius=4.5 StartAngle=4.71239 EndAngle=7.85398
    g5: Circle CenterX=0 CenterY=0 CenterZ=0 NormalX=0 NormalY=0 NormalZ=1 AngleXU=0 Radius=1.65
    g6: LineSegment StartX=0 StartY=-6 StartZ=0 EndX=0 EndY=0 EndZ=0
  constraints (18):
    c: Coincident(g0,g-1)
    c: PointOnObject(g0,g-1)
    c: PointOnObject(g0,g-1)
    c: Tangent(g0,g1) = -1.5708
    c: Coincident(g1,g2)
    c: Horizontal(g2)
    c: PointOnObject(g3,g-1)
    c: Coincident(g3,g0)
    c: Distance(g1) = 9
    c: Distance(g2) = 9
    c: Radius(g0) = 3.15
    c: Tangent(g4,g2) = -1.5708
    c: Tangent(g4,g3) = -1.5708
    c: Coincident(g5,g0)
    c: Diameter(g5) = 3.3
    c: PointOnObject(g6,g-2)
    c: Coincident(g6,g0)
    c: Distance(g6) = 6  'y0'
FEATURE [PartDesign::Pad] Pad197
  Direction = (0,0,1)
  Length = 11
  Length2 = 10
  Profile = -> Sketch321
  ReferenceAxis = -> Sketch321 [N_Axis]
  Type = 0
FEATURE [Sketcher::SketchObject] Sketch322
  AttachmentOffset = pos=(0,0,-4) rot=(0,0,1;0rad)
  FullyConstrained = true
  MapMode = 5
  Placement = pos=(-4,9e-16,-9e-16) rot=(0.57735,0.57735,0.57735;2.0944rad)
  Support = -> [YZ_Plane136]
  expr: Constraints[2] = 3 + 2 * <<BaseParameters>>.axisTolerance
  sketch-geometry (1):
    g0: Circle CenterX=-6 CenterY=0 CenterZ=0 NormalX=0 NormalY=0 NormalZ=1 AngleXU=0 Radius=1.65
  constraints (3):
    c: PointOnObject(g0,g-1)
    c: Distance(g0,g-2) = 6
    c: Diameter(g0) = 3.3
FEATURE [PartDesign::Pocket] Pocket114
  BaseFeature = -> Pad197
  Direction = (-1,2e-16,-3e-16)
  Length = 12
  Length2 = 5
  Profile = -> Sketch322
  ReferenceAxis = -> Sketch322 [N_Axis]
  Reversed = true
  Type = 0
FEATURE [Sketcher::SketchObject] Sketch323
  AttachmentOffset = pos=(0,0,1.5) rot=(0,0,1;0rad)
  FullyConstrained = true
  MapMode = 5
  Placement = pos=(0,0,1.5) rot=(0,0,1;0rad)
  Support = -> [XY_Plane136]
  expr: .AttachmentOffset.Base.z = <<BaseParameters>>.joystickArmZoffset
  expr: Constraints[11] = 3 + <<BaseParameters>>.tolerance
  sketch-geometry (5):
    g0: LineSegment StartX=-4 StartY=-3.15 StartZ=0 EndX=-4e-16 EndY=-3.15 EndZ=0
    g1: ArcOfCircle CenterX=0 CenterY=-2.13e-14 CenterZ=0 NormalX=0 NormalY=0 NormalZ=1 AngleXU=0 Radius=3.15 StartAngle=4.71239 EndAngle=6.28319
    g2: LineSegment StartX=3.15 StartY=3e-16 StartZ=0 EndX=3.15 EndY=4 EndZ=0
    g3: LineSegment StartX=3.15 StartY=4 StartZ=0 EndX=-4 EndY=4 EndZ=0
    g4: LineSegment StartX=-4 StartY=4 StartZ=0 EndX=-4 EndY=-3.15 EndZ=0
  constraints (14):
    c: PointOnObject(g0,g-2)
    c: Tangent(g0,g1) = -1.5708
    c: PointOnObject(g1,g-1)
    c: Tangent(g1,g2) = -1.5708
    c: Coincident(g2,g3)
    c: Horizontal(g3)
    c: Coincident(g3,g4)
    c: Coincident(g4,g0)
    c: Vertical(g4)
    c: Vertical(g2)
    c: Horizontal(g0)
    c: Radius(g1) = 3.15
    c: Distance(g0) = 4
    c: Distance(g2) = 4
FEATURE [PartDesign::Pocket] Pocket115
  BaseFeature = -> Pocket114
  Direction = (0,0,-1)
  Length = 6.3
  Length2 = 5
  Midplane = true
  Profile = -> Sketch323
  ReferenceAxis = -> Sketch323 [N_Axis]
  Type = 0
  expr: Length = 6 + 2 * <<BaseParameters>>.tolerance
FEATURE [Sketcher::SketchObject] Sketch324
  FullyConstrained = true
  MapMode = 5
  Placement = pos=(0,0,0) rot=(1,0,0;1.5708rad)
  Support = -> [XZ_Plane136]
  expr: Constraints[10] = 3 + <<BaseParameters>>.tolerance
  sketch-geometry (4):
    g0: LineSegment StartX=3.15 StartY=7 StartZ=0 EndX=11 EndY=7 EndZ=0
    g1: LineSegment StartX=11 StartY=7 StartZ=0 EndX=11 EndY=4 EndZ=0
    g2: LineSegment StartX=11 StartY=4 StartZ=0 EndX=6.15 EndY=4 EndZ=0
    g3: LineSegment StartX=6.15 StartY=4 StartZ=0 EndX=3.15 EndY=7 EndZ=0
  constraints (12):
    c: Coincident(g0,g1)
    c: Coincident(g1,g2)
    c: Coincident(g2,g3)
    c: Coincident(g3,g0)
    c: Horizontal(g0)
    c: Horizontal(g2)
    c: Vertical(g1)
    c: Distance(g1,g-1) = 4
    c: Distance(g1) = 3
    c: Angle(g3,g0) = 0.785398
    c: Distance(g0,g-2) = 3.15
    c: Distance(g0,g-2) = 11
FEATURE [PartDesign::Pocket] Pocket116
  BaseFeature = -> Pocket115
  Direction = (0,1,2e-16)
  Length = 14
  Length2 = 5
  Profile = -> Sketch324
  ReferenceAxis = -> Sketch324 [N_Axis]
  Reversed = true
  Type = 0
FEATURE [PartDesign::Body] Body090  label="JoystickBaseStructure0"
  Group = -> [Sketch321,Pad197,Sketch322,Pocket114,Sketch323,Pocket115,Sketch324,Pocket116]
  Origin = -> Origin136
  Placement = pos=(82.171,-50.2883,0) rot=(0,0,-1;0.003689rad)
  Tip = -> Pocket116
  expr: .Placement.Base.x = Sketch301.Constraints.x1
  expr: .Placement.Base.y = -Sketch301.Constraints.y1
  expr: .Placement.Rotation.Angle = 180deg - Sketch301.Constraints.theta1
FEATURE [Sketcher::SketchObject] Sketch325
  FullyConstrained = true
  MapMode = 5
  Placement = pos=(0,0,0) rot=(0.57735,0.57735,0.57735;2.0944rad)
  Support = -> [YZ_Plane137]
  sketch-geometry (1):
    g0: Circle CenterX=0 CenterY=0 CenterZ=0 NormalX=0 NormalY=0 NormalZ=1 AngleXU=0 Radius=1.5
  constraints (2):
    c: Coincident(g0,g-1)
    c: Diameter(g0) = 3
FEATURE [PartDesign::Pad] Pad198
  Direction = (1,-2e-16,3e-16)
  Length = 170
  Length2 = 10
  Placement = pos=(0,0,0) rot=(0.57735,0.57735,0.57735;2.0944rad)
  Profile = -> Sketch325
  ReferenceAxis = -> Sketch325 [N_Axis]
  Reversed = true
  Type = 0
  expr: Length = <<BaseParameters>>.joystickBaseArm2Length
FEATURE [PartDesign::Body] Body091  label="JoystickBaseArm2"
  Group = -> [Sketch325,Pad198]
  Origin = -> Origin137
  Placement = pos=(90.1488,-56.3178,0) rot=(0,0,-1;0.003689rad)
  Tip = -> Pad198
  expr: .Placement.Base.x = Sketch301.Constraints.x3
  expr: .Placement.Base.y = -Sketch301.Constraints.y3
  expr: .Placement.Rotation.Angle = 180deg - Sketch301.Constraints.theta1
FEATURE [Sketcher::SketchObject] Sketch326
  FullyConstrained = true
  MapMode = 5
  Placement = pos=(0,0,0) rot=(1,0,0;1.5708rad)
  Support = -> [XZ_Plane138]
  expr: Constraints[20] = 6 + <<BaseParameters>>.tolerance
  expr: Constraints[22] = <<BaseParameters>>.joystickArmZoffset
  expr: Constraints[25] = 6 + 2 * <<BaseParameters>>.tolerance
  sketch-geometry (11):
    g0: LineSegment StartX=-10 StartY=4 StartZ=0 EndX=-10 EndY=-4 EndZ=0
    g1: LineSegment StartX=-10 StartY=-4 StartZ=0 EndX=9.15 EndY=-4 EndZ=0
    g2: LineSegment StartX=9.15 StartY=-4 StartZ=0 EndX=9.15 EndY=-1.65 EndZ=0
    g3: LineSegment StartX=9.15 StartY=-1.65 StartZ=0 EndX=3 EndY=-1.65 EndZ=0
    g4: LineSegment StartX=3 StartY=-1.65 StartZ=0 EndX=3 EndY=4.65 EndZ=0
    g5: LineSegment StartX=3 StartY=4.65 StartZ=0 EndX=9.15 EndY=4.65 EndZ=0
    g6: LineSegment StartX=9.15 StartY=4.65 StartZ=0 EndX=9.15 EndY=7 EndZ=0
    g7: LineSegment StartX=9.15 StartY=7 StartZ=0 EndX=0 EndY=7 EndZ=0
    g8: LineSegment StartX=0 StartY=7 StartZ=0 EndX=-3 EndY=4 EndZ=0
    g9: LineSegment StartX=-3 StartY=4 StartZ=0 EndX=-10 EndY=4 EndZ=0
    g10: GeomPoint X=3 Y=1.5 Z=0
  constraints (30):
    c: Coincident(g0,g1)
    c: Horizontal(g1)
    c: Coincident(g1,g2)
    c: Vertical(g2)
    c: Coincident(g2,g3)
    c: Horizontal(g3)
    c: Coincident(g3,g4)
    c: Coincident(g4,g5)
    c: Horizontal(g5)
    c: Coincident(g5,g6)
    c: Vertical(g6)
    c: Coincident(g6,g7)
    c: Horizontal(g7)
    c: Coincident(g7,g8)
    c: Coincident(g8,g9)
    c: Coincident(g9,g0)
    c: Horizontal(g9)
    c: Symmetric(g0,g0,g-1)
    c: Distance(g0,g-2) = 10
    c: Distance(g-1,g4) = 3
    c: Distance(g3) = 6.15
    c: Equal(g5,g3)
    c: Distance(g10,g-1) = 1.5
    c: Symmetric(g4,g3,g10)
    c: Vertical(g4)
    c: Distance(g4) = 6.3
    c: Distance(g0) = 8
    c: Equal(g6,g2)
    c: Angle(g8,g9) = 2.35619
    c: PointOnObject(g7,g-2)
FEATURE [PartDesign::Pad] Pad199
  Direction = (0,-1,-2e-16)
  Length = 6
  Length2 = 10
  Midplane = true
  Placement = pos=(0,0,0) rot=(1,0,0;1.5708rad)
  Profile = -> Sketch326
  ReferenceAxis = -> Sketch326 [N_Axis]
  Type = 0
FEATURE [Sketcher::SketchObject] Sketch327
  FullyConstrained = true
  MapMode = 5
  Placement = pos=(0,0,0) rot=(0.57735,0.57735,0.57735;2.0944rad)
  Support = -> [YZ_Plane138]
  expr: Constraints[1] = 3 + 2 * <<BaseParameters>>.axisTolerance
  sketch-geometry (1):
    g0: Circle CenterX=0 CenterY=0 CenterZ=0 NormalX=0 NormalY=0 NormalZ=1 AngleXU=0 Radius=1.65
  constraints (2):
    c: Coincident(g0,g-1)
    c: Diameter(g0) = 3.3
FEATURE [PartDesign::Pocket] Pocket117
  BaseFeature = -> Pad199
  Direction = (-1,2e-16,-3e-16)
  Length = 10
  Length2 = 5
  Placement = pos=(0,0,0) rot=(1,0,0;1.5708rad)
  Profile = -> Sketch327
  ReferenceAxis = -> Sketch327 [N_Axis]
  Type = 0
FEATURE [Sketcher::SketchObject] Sketch328
  FullyConstrained = true
  MapMode = 5
  Support = -> [XY_Plane138]
  expr: Constraints[19] = 3 + 2 * <<BaseParameters>>.axisTolerance
  expr: Constraints[1] = 6 + <<BaseParameters>>.tolerance
  sketch-geometry (7):
    g0: Circle CenterX=6.15 CenterY=0 CenterZ=0 NormalX=0 NormalY=0 NormalZ=1 AngleXU=0 Radius=1.65
    g1: LineSegment StartX=6.15 StartY=3 StartZ=0 EndX=6.15 EndY=4 EndZ=0
    g2: LineSegment StartX=6.15 StartY=4 StartZ=0 EndX=10.15 EndY=4 EndZ=0
    g3: LineSegment StartX=10.15 StartY=4 StartZ=0 EndX=10.15 EndY=-4 EndZ=0
    g4: LineSegment StartX=10.15 StartY=-4 StartZ=0 EndX=6.15 EndY=-4 EndZ=0
    g5: LineSegment StartX=6.15 StartY=-4 StartZ=0 EndX=6.15 EndY=-3 EndZ=0
    g6: ArcOfCircle CenterX=6.15 CenterY=0 CenterZ=0 NormalX=0 NormalY=0 NormalZ=1 AngleXU=0 Radius=3 StartAngle=4.71239 EndAngle=7.85398
  constraints (20):
    c: PointOnObject(g0,g-1)
    c: Distance(g0,g-2) = 6.15
    c: Vertical(g1)
    c: Coincident(g1,g2)
    c: Horizontal(g2)
    c: Coincident(g2,g3)
    c: Coincident(g3,g4)
    c: Horizontal(g4)
    c: Coincident(g4,g5)
    c: Vertical(g5)
    c: Coincident(g6,g0)
    c: Coincident(g6,g1)
    c: Coincident(g6,g5)
    c: Radius(g6) = 3
    c: Distance(g1) = 1
    c: Distance(g2) = 4
    c: Symmetric(g2,g3,g-1)
    c: Perpendicular(g6,g1)
    c: Perpendicular(g6,g5)
    c: Diameter(g0) = 3.3
FEATURE [PartDesign::Pocket] Pocket118
  BaseFeature = -> Pocket117
  Direction = (0,0,-1)
  Length = 16
  Length2 = 5
  Midplane = true
  Placement = pos=(0,0,0) rot=(1,0,0;1.5708rad)
  Profile = -> Sketch328
  ReferenceAxis = -> Sketch328 [N_Axis]
  Type = 0
FEATURE [PartDesign::Body] Body092  label="JoystickBaseStructure1"
  Group = -> [Sketch326,Pad199,Sketch327,Pocket117,Sketch328,Pocket118]
  Origin = -> Origin138
  Placement = pos=(-79.85,-55.6906,0) rot=(0,0,1;3.1379rad)
  Tip = -> Pocket118
  expr: .Placement.Base.x = -Sketch301.Constraints.x4
  expr: .Placement.Base.y = -Sketch301.Constraints.y4
  expr: .Placement.Rotation.Angle = Sketch301.Constraints.theta1
FEATURE [Sketcher::SketchObject] Sketch329
  FullyConstrained = true
  MapMode = 5
  Support = -> [XY_Plane139]
  expr: Constraints[11] = 3 + 2 * <<BaseParameters>>.axisTolerance
  sketch-geometry (5):
    g0: Circle CenterX=0 CenterY=0 CenterZ=0 NormalX=0 NormalY=0 NormalZ=1 AngleXU=0 Radius=1.65
    g1: LineSegment StartX=-3 StartY=4e-16 StartZ=0 EndX=-3 EndY=7 EndZ=0
    g2: LineSegment StartX=-3 StartY=7 StartZ=0 EndX=3 EndY=7 EndZ=0
    g3: LineSegment StartX=3 StartY=7 StartZ=0 EndX=3 EndY=-9e-16 EndZ=0
    g4: ArcOfCircle CenterX=0 CenterY=0 CenterZ=0 NormalX=0 NormalY=0 NormalZ=1 AngleXU=0 Radius=3 StartAngle=3.14159 EndAngle=6.28319
  constraints (14):
    c: Coincident(g0,g-1)
    c: PointOnObject(g1,g-1)
    c: Vertical(g1)
    c: Coincident(g1,g2)
    c: Horizontal(g2)
    c: Coincident(g2,g3)
    c: PointOnObject(g3,g-1)
    c: Vertical(g3)
    c: Coincident(g4,g0)
    c: Coincident(g4,g1)
    c: Coincident(g4,g3)
    c: Diameter(g0) = 3.3
    c: Radius(g4) = 3
    c: Distance(g3) = 7
FEATURE [PartDesign::Pad] Pad200
  Direction = (0,0,1)
  Length = 6
  Length2 = 10
  Midplane = true
  Profile = -> Sketch329
  ReferenceAxis = -> Sketch329 [N_Axis]
  Type = 0
FEATURE [Sketcher::SketchObject] Sketch330
  FullyConstrained = true
  MapMode = 5
  Placement = pos=(0,0,0) rot=(1,0,0;1.5708rad)
  Support = -> [XZ_Plane139]
  expr: Constraints[1] = 3 + <<BaseParameters>>.axisTolerance * 2
  sketch-geometry (1):
    g0: Circle CenterX=0 CenterY=0 CenterZ=0 NormalX=0 NormalY=0 NormalZ=1 AngleXU=0 Radius=1.65
  constraints (2):
    c: Coincident(g0,g-1)
    c: Diameter(g0) = 3.3
FEATURE [PartDesign::Pocket] Pocket119
  BaseFeature = -> Pad200
  Direction = (0,1,2e-16)
  Length = 7
  Length2 = 5
  Profile = -> Sketch330
  ReferenceAxis = -> Sketch330 [N_Axis]
  Type = 0
FEATURE [PartDesign::Body] Body093  label="JoystickBaseHinge2"
  Group = -> [Sketch329,Pad200,Sketch330,Pocket119]
  Origin = -> Origin139
  Placement = pos=(-86,-55.6679,1.5) rot=(0,0,1;0rad)
  Tip = -> Pocket119
  expr: .Placement.Base.x = -Sketch301.Constraints.x5
  expr: .Placement.Base.y = -Sketch301.Constraints.y5
  expr: .Placement.Base.z = <<BaseParameters>>.joystickArmZoffset
FEATURE [Sketcher::SketchObject] Sketch331
  FullyConstrained = true
  MapMode = 5
  Placement = pos=(0,0,0) rot=(1,0,0;1.5708rad)
  Support = -> [XZ_Plane140]
  sketch-geometry (1):
    g0: Circle CenterX=0 CenterY=0 CenterZ=0 NormalX=0 NormalY=0 NormalZ=1 AngleXU=0 Radius=1.5
  constraints (2):
    c: Coincident(g0,g-1)
    c: Diameter(g0) = 3
FEATURE [PartDesign::Pad] Pad201
  Direction = (0,-1,-2e-16)
  Length = 80
  Length2 = 10
  Placement = pos=(0,0,0) rot=(1,0,0;1.5708rad)
  Profile = -> Sketch331
  ReferenceAxis = -> Sketch331 [N_Axis]
  Reversed = true
  Type = 0
  expr: Length = <<BaseParameters>>.joystickBaseArm1Length
FEATURE [PartDesign::Body] Body094  label="JoystickBaseArm1"
  Group = -> [Sketch331,Pad201]
  Origin = -> Origin140
  Placement = pos=(-86,-54.0179,1.5) rot=(0,0,1;0rad)
  Tip = -> Pad201
  expr: .Placement.Base.x = -Sketch301.Constraints.x5
  expr: .Placement.Base.y = -Sketch301.Constraints.y5 + (1.5 + <<BaseParameters>>.axisTolerance) * 1mm
  expr: .Placement.Base.z = <<BaseParameters>>.joystickArmZoffset
FEATURE [Sketcher::SketchObject] Sketch332
  AttachmentOffset = pos=(0,0,-4) rot=(0,0,1;0rad)
  FullyConstrained = true
  MapMode = 5
  Placement = pos=(0,0,-4) rot=(0,0,1;0rad)
  Support = -> [XY_Plane141]
  sketch-geometry (4):
    g0: LineSegment StartX=5 StartY=-7 StartZ=0 EndX=-13 EndY=-7 EndZ=0
    g1: LineSegment StartX=-13 StartY=-7 StartZ=0 EndX=-13 EndY=3 EndZ=0
    g2: LineSegment StartX=-13 StartY=3 StartZ=0 EndX=5 EndY=3 EndZ=0
    g3: LineSegment StartX=5 StartY=3 StartZ=0 EndX=5 EndY=-7 EndZ=0
  constraints (12):
    c: Coincident(g0,g1)
    c: Coincident(g1,g2)
    c: Coincident(g2,g3)
    c: Coincident(g3,g0)
    c: Horizontal(g0)
    c: Horizontal(g2)
    c: Vertical(g1)
    c: Distance(g3) = 10
    c: Distance(g0,g-2) = 13
    c: Distance(g0,g-2) = 5
    c: Distance(g2,g-1) = 3
    c: Vertical(g3)
FEATURE [PartDesign::Pad] Pad202
  Direction = (0,0,1)
  Length = 11
  Length2 = 10
  Profile = -> Sketch332
  ReferenceAxis = -> Sketch332 [N_Axis]
  Type = 0
FEATURE [Sketcher::SketchObject] Sketch333
  AttachmentOffset = pos=(0,0,-3) rot=(0,0,1;0rad)
  FullyConstrained = true
  MapMode = 5
  Placement = pos=(0,3,7e-16) rot=(1,0,0;1.5708rad)
  Support = -> [XZ_Plane141]
  expr: Constraints[10] = <<BaseParameters>>.joystickArmZoffset + 3
  expr: Constraints[1] = 3 + 2 * <<BaseParameters>>.axisTolerance
  sketch-geometry (5):
    g0: Circle CenterX=0 CenterY=0 CenterZ=0 NormalX=0 NormalY=0 NormalZ=1 AngleXU=0 Radius=1.65
    g1: LineSegment StartX=-13 StartY=4.5 StartZ=0 EndX=-7.5 EndY=4.5 EndZ=0
    g2: LineSegment StartX=-7.5 StartY=4.5 StartZ=0 EndX=-5 EndY=7 EndZ=0
    g3: LineSegment StartX=-5 StartY=7 StartZ=0 EndX=-13 EndY=7 EndZ=0
    g4: LineSegment StartX=-13 StartY=7 StartZ=0 EndX=-13 EndY=4.5 EndZ=0
  constraints (14):
    c: Coincident(g0,g-1)
    c: Diameter(g0) = 3.3
    c: Horizontal(g1)
    c: Coincident(g1,g2)
    c: Coincident(g2,g3)
    c: Horizontal(g3)
    c: Coincident(g3,g4)
    c: Coincident(g4,g1)
    c: Vertical(g4)
    c: Distance(g2,g-2) = 5
    c: Distance(g1,g-1) = 4.5
    c: Distance(g3,g-2) = 13
    c: Angle(g3,g2) = 0.785398
    c: Distance(g3,g-1) = 7
FEATURE [PartDesign::Pocket] Pocket120
  BaseFeature = -> Pad202
  Direction = (0,1,2e-16)
  Length = 10
  Length2 = 5
  Profile = -> Sketch333
  ReferenceAxis = -> Sketch333 [N_Axis]
  Reversed = true
  Type = 0
FEATURE [Sketcher::SketchObject] Sketch334
  FullyConstrained = true
  MapMode = 5
  Placement = pos=(0,0,0) rot=(1,0,0;1.5708rad)
  Support = -> [XZ_Plane141]
  expr: Constraints[1] = <<BaseParameters>>.joystickArmZoffset
  expr: Constraints[2] = 3 + 2 * <<BaseParameters>>.axisTolerance
  sketch-geometry (1):
    g0: Circle CenterX=-10 CenterY=1.5 CenterZ=0 NormalX=0 NormalY=0 NormalZ=1 AngleXU=0 Radius=1.65
  constraints (3):
    c: Distance(g0,g-2) = 10
    c: Distance(g0,g-1) = 1.5
    c: Diameter(g0) = 3.3
FEATURE [PartDesign::Pocket] Pocket121
  BaseFeature = -> Pocket120
  Direction = (0,1,2e-16)
  Length = 7
  Length2 = 5
  Profile = -> Sketch334
  ReferenceAxis = -> Sketch334 [N_Axis]
  Reversed = true
  Type = 0
FEATURE [Sketcher::SketchObject] Sketch335
  AttachmentOffset = pos=(0,0,4) rot=(0,0,1;0rad)
  FullyConstrained = true
  MapMode = 5
  Placement = pos=(0,0,4) rot=(0,0,1;0rad)
  Support = -> [XY_Plane141]
  sketch-geometry (10):
    g0: LineSegment StartX=3.23316 StartY=-2 StartZ=0 EndX=1.61658 EndY=0.8 EndZ=0
    g1: LineSegment StartX=1.61658 StartY=0.8 StartZ=0 EndX=-1.61658 EndY=0.8 EndZ=0
    g2: LineSegment StartX=-1.61658 StartY=0.8 StartZ=0 EndX=-3.23316 EndY=-2 EndZ=0
    g3: LineSegment StartX=-3.23316 StartY=-2 StartZ=0 EndX=-1.61658 EndY=-4.8 EndZ=0
    g4: LineSegment StartX=-1.61658 StartY=-4.8 StartZ=0 EndX=1.61658 EndY=-4.8 EndZ=0
    g5: LineSegment StartX=1.61658 StartY=-4.8 StartZ=0 EndX=3.23316 EndY=-2 EndZ=0
    g6: Circle CenterX=0 CenterY=-2 CenterZ=0 NormalX=0 NormalY=0 NormalZ=1 AngleXU=0 Radius=3.23316
    g7: LineSegment StartX=1.61658 StartY=0.8 StartZ=0 EndX=5.61658 EndY=0.8 EndZ=0
    g8: LineSegment StartX=5.61658 StartY=0.8 StartZ=0 EndX=5.61658 EndY=-4.8 EndZ=0
    g9: LineSegment StartX=5.61658 StartY=-4.8 StartZ=0 EndX=1.61658 EndY=-4.8 EndZ=0
  constraints (25):
    c: Coincident(g0,g1)
    c: Coincident(g1,g2)
    c: Coincident(g2,g3)
    c: Coincident(g3,g4)
    c: Coincident(g4,g5)
    c: Coincident(g5,g0)
    c: Equal(g0, g1-g5) x5
    c: PointOnObject(g0,g6)
    c: PointOnObject(g1,g6)
    c: PointOnObject(g2,g6)
    c: PointOnObject(g3,g6)
    c: PointOnObject(g4,g6)
    c: PointOnObject(g5,g6)
    c: PointOnObject(g6,g-2)
    c: Horizontal(g1)
    c: Distance(g1,g3) = 5.6
    c: Distance(g6,g-1) = 2
    c: Coincident(g0,g7)
    c: Horizontal(g7)
    c: Coincident(g7,g8)
    c: Vertical(g8)
    c: Coincident(g8,g9)
    c: Coincident(g9,g4)
    c: Horizontal(g9)
    c: Distance(g7) = 4
FEATURE [PartDesign::Pocket] Pocket122
  BaseFeature = -> Pocket121
  Direction = (0,0,-1)
  Length = 2.6
  Length2 = 5
  Midplane = true
  Profile = -> Sketch335
  ReferenceAxis = -> Sketch335 [N_Axis]
  Type = 0
FEATURE [Sketcher::SketchObject] Sketch336
  FullyConstrained = true
  MapMode = 5
  Support = -> [XY_Plane141]
  expr: Constraints[2] = 3 + 2 * <<BaseParameters>>.screwHoleTolerance
  sketch-geometry (1):
    g0: Circle CenterX=0 CenterY=-2 CenterZ=0 NormalX=0 NormalY=0 NormalZ=1 AngleXU=0 Radius=1.6
  constraints (3):
    c: PointOnObject(g0,g-2)
    c: Distance(g0,g-1) = 2
    c: Diameter(g0) = 3.2
FEATURE [PartDesign::Pocket] Pocket123
  BaseFeature = -> Pocket122
  Direction = (0,0,-1)
  Length = 10
  Length2 = 5
  Profile = -> Sketch336
  ReferenceAxis = -> Sketch336 [N_Axis]
  Reversed = true
  Type = 0
FEATURE [PartDesign::Body] Body095  label="JoystickBaseSlider1"
  Group = -> [Sketch332,Pad202,Sketch333,Pocket120,Sketch334,Pocket121,Sketch335,Pocket122,Sketch336,Pocket123]
  Origin = -> Origin141
  Placement = pos=(-76,25.9821,0) rot=(0,0,1;0rad)
  Tip = -> Pocket123
  expr: .Placement.Base.x = -Sketch301.Constraints.x6
  expr: .Placement.Base.y = Sketch301.Constraints.y6
FEATURE [Sketcher::SketchObject] Sketch347
  AttachmentOffset = pos=(0,0,-6) rot=(0,0,1;0rad)
  FullyConstrained = true
  MapMode = 5
  Placement = pos=(-6,1.3e-15,-1.3e-15) rot=(0.57735,0.57735,0.57735;2.0944rad)
  Support = -> [YZ_Plane127]
  expr: Constraints[11] = 3 + 2 * <<BaseParameters>>.axisTolerance
  expr: Constraints[12] = 3 + <<BaseParameters>>.tolerance
  sketch-geometry (5):
    g0: LineSegment StartX=-7 StartY=3 StartZ=0 EndX=3 EndY=3 EndZ=0
    g1: LineSegment StartX=3 StartY=3 StartZ=0 EndX=3 EndY=6.15 EndZ=0
    g2: ArcOfCircle CenterX=0 CenterY=6.15 CenterZ=0 NormalX=0 NormalY=0 NormalZ=1 AngleXU=0 Radius=3 StartAngle=0 EndAngle=2.39518
    g3: LineSegment StartX=-2.20238 StartY=8.18704 StartZ=0 EndX=-7 EndY=3 EndZ=0
    g4: Circle CenterX=0 CenterY=6.15 CenterZ=0 NormalX=0 NormalY=0 NormalZ=1 AngleXU=0 Radius=1.65
  constraints (13):
    c: Horizontal(g0)
    c: Coincident(g0,g1)
    c: Vertical(g1)
    c: Tangent(g1,g2) = -1.5708
    c: Tangent(g2,g3) = -1.5708
    c: Coincident(g3,g0)
    c: Distance(g0,g-1) = 3
    c: Distance(g0,g-2) = 3
    c: Distance(g0,g-2) = 7
    c: Coincident(g4,g2)
    c: PointOnObject(g2,g-2)
    c: Diameter(g4) = 3.3
    c: Distance(g2,g0) = 3.15
FEATURE [PartDesign::Pad] Pad208
  BaseFeature = -> Pocket106
  Direction = (1,-2e-16,3e-16)
  Length = 11
  Length2 = 10
  Placement = pos=(0,0,0) rot=(0.57735,0.57735,0.57735;2.0944rad)
  Profile = -> Sketch347
  ReferenceAxis = -> Sketch347 [N_Axis]
  Type = 0
FEATURE [Sketcher::SketchObject] Sketch357
  FullyConstrained = false
  MapMode = 5
  Placement = pos=(0,0,0) rot=(0.57735,0.57735,0.57735;2.0944rad)
  Support = -> [YZ_Plane106]
  sketch-geometry (7):
    g0: LineSegment StartX=0 StartY=0 StartZ=0 EndX=80.0705 EndY=0 EndZ=0
    g1: LineSegment StartX=80.0705 StartY=0 StartZ=0 EndX=80.0705 EndY=6.24829 EndZ=0
    g2: LineSegment StartX=80.0705 StartY=6.24829 StartZ=0 EndX=87.0267 EndY=68.9938 EndZ=0
    g3: LineSegment StartX=18.5592 StartY=0 StartZ=0 EndX=18.5592 EndY=6.01981 EndZ=0
    g4: LineSegment StartX=18.5592 StartY=6.01981 StartZ=0 EndX=-2.1084 EndY=27.6035 EndZ=0
    g5: LineSegment StartX=-2.1084 StartY=27.6035 StartZ=0 EndX=39.2263 EndY=33.68 EndZ=0
    g6: LineSegment StartX=39.2263 StartY=33.68 StartZ=0 EndX=67.7306 EndY=59.9716 EndZ=0
  constraints (10):
    c: Coincident(g0,g-1)
    c: PointOnObject(g0,g-1)
    c: Coincident(g0,g1)
    c: Vertical(g1)
    c: Coincident(g1,g2)
    c: PointOnObject(g3,g0)
    c: Vertical(g3)
    c: Coincident(g3,g4)
    c: Coincident(g4,g5)
    c: Coincident(g5,g6)
FEATURE [Sketcher::SketchObject] Sketch392
  FullyConstrained = true
  MapMode = 5
  Placement = pos=(0,0,0) rot=(1,0,0;1.5708rad)
  Support = -> [XZ_Plane109]
  sketch-geometry (8):
    g0: LineSegment StartX=-10 StartY=10 StartZ=0 EndX=-3 EndY=10 EndZ=0
    g1: LineSegment StartX=-3 StartY=10 StartZ=0 EndX=-3 EndY=3 EndZ=0
    g2: LineSegment StartX=-3 StartY=3 StartZ=0 EndX=-10 EndY=3 EndZ=0
    g3: LineSegment StartX=-10 StartY=3 StartZ=0 EndX=-10 EndY=10 EndZ=0
    g4: LineSegment StartX=3 StartY=10 StartZ=0 EndX=10 EndY=10 EndZ=0
    g5: LineSegment StartX=10 StartY=10 StartZ=0 EndX=10 EndY=3 EndZ=0
    g6: LineSegment StartX=10 StartY=3 StartZ=0 EndX=3 EndY=3 EndZ=0
    g7: LineSegment StartX=3 StartY=3 StartZ=0 EndX=3 EndY=10 EndZ=0
  constraints (23):
    c: Coincident(g0,g1)
    c: Coincident(g1,g2)
    c: Coincident(g2,g3)
    c: Coincident(g3,g0)
    c: Horizontal(g0)
    c: Horizontal(g2)
    c: Vertical(g1)
    c: Vertical(g3)
    c: Coincident(g4,g5)
    c: Coincident(g5,g6)
    c: Coincident(g6,g7)
    c: Coincident(g7,g4)
    c: Horizontal(g4)
    c: Horizontal(g6)
    c: Vertical(g5)
    c: Vertical(g7)
    c: Distance(g1,g-1) = 3
    c: Symmetric(g1,g6,g-2)
    c: Equal(g0,g4)
    c: Distance(g2,g5) = 20
    c: Distance(g3) = 7
    c: Equal(g3,g7)
    c: Distance(g1,g6) = 6
FEATURE [PartDesign::Pocket] Pocket157
  BaseFeature = -> Pocket087
  Direction = (0,1,2e-16)
  Length = 14
  Length2 = 5
  Midplane = true
  Placement = pos=(0,0,0) rot=(0.57735,0.57735,0.57735;2.0944rad)
  Profile = -> Sketch392
  ReferenceAxis = -> Sketch392 [N_Axis]
  Type = 0
FEATURE [Sketcher::SketchObject] Sketch393
  FullyConstrained = true
  MapMode = 5
  Placement = pos=(0,0,0) rot=(0.57735,0.57735,0.57735;2.0944rad)
  Support = -> [YZ_Plane194]
  sketch-geometry (2):
    g0: ArcOfCircle CenterX=0 CenterY=0 CenterZ=0 NormalX=0 NormalY=0 NormalZ=1 AngleXU=0 Radius=3 StartAngle=3.14159 EndAngle=6.28319
    g1: LineSegment StartX=-3 StartY=4e-16 StartZ=0 EndX=3 EndY=-7e-16 EndZ=0
  constraints (6):
    c: Coincident(g0,g-1)
    c: PointOnObject(g0,g-1)
    c: PointOnObject(g0,g-1)
    c: Coincident(g1,g0)
    c: Coincident(g1,g0)
    c: Radius(g0) = 3
FEATURE [PartDesign::Pad] Pad227
  Direction = (1,-2e-16,3e-16)
  Length = 19
  Length2 = 10
  Midplane = true
  Placement = pos=(0,0,0) rot=(0.57735,0.57735,0.57735;2.0944rad)
  Profile = -> Sketch393
  ReferenceAxis = -> Sketch393 [N_Axis]
  Type = 0
FEATURE [Sketcher::SketchObject] Sketch394
  FullyConstrained = true
  MapMode = 5
  Support = -> [XY_Plane194]
  sketch-geometry (4):
    g0: LineSegment StartX=-9.5 StartY=3 StartZ=0 EndX=9.5 EndY=3 EndZ=0
    g1: LineSegment StartX=9.5 StartY=3 StartZ=0 EndX=9.5 EndY=-3 EndZ=0
    g2: LineSegment StartX=9.5 StartY=-3 StartZ=0 EndX=-9.5 EndY=-3 EndZ=0
    g3: LineSegment StartX=-9.5 StartY=-3 StartZ=0 EndX=-9.5 EndY=3 EndZ=0
  constraints (11):
    c: Coincident(g0,g1)
    c: Coincident(g1,g2)
    c: Coincident(g2,g3)
    c: Coincident(g3,g0)
    c: Horizontal(g0)
    c: Horizontal(g2)
    c: Vertical(g1)
    c: Vertical(g3)
    c: Symmetric(g0,g1,g-1)
    c: Distance(g0) = 19
    c: Distance(g1) = 6
FEATURE [Sketcher::SketchObject] Sketch395
  AttachmentOffset = pos=(0,0,8) rot=(0,0,1;0rad)
  FullyConstrained = true
  MapMode = 5
  Placement = pos=(0,0,8) rot=(0,0,1;0rad)
  Support = -> [XY_Plane194]
  sketch-geometry (4):
    g0: ArcOfCircle CenterX=-5 CenterY=0 CenterZ=0 NormalX=0 NormalY=0 NormalZ=1 AngleXU=0 Radius=3 StartAngle=1.5708 EndAngle=4.71239
    g1: ArcOfCircle CenterX=5 CenterY=0 CenterZ=0 NormalX=0 NormalY=0 NormalZ=1 AngleXU=0 Radius=3 StartAngle=4.71239 EndAngle=7.85398
    g2: LineSegment StartX=-5 StartY=-3 StartZ=0 EndX=5 EndY=-3 EndZ=0
    g3: LineSegment StartX=5 StartY=3 StartZ=0 EndX=-5 EndY=3 EndZ=0
  constraints (9):
    c: Tangent(g0,g2) = -1.5708
    c: Tangent(g2,g1) = -1.5708
    c: Tangent(g1,g3) = -1.5708
    c: Tangent(g3,g0) = -1.5708
    c: Equal(g0,g1)
    c: PointOnObject(g0,g-1)
    c: Distance(g0,g1) = 10
    c: Symmetric(g0,g1,g-2)
    c: Radius(g1) = 3
FEATURE [PartDesign::AdditiveLoft] AdditiveLoft002
  BaseFeature = -> Pad227
  Closed = false
  Placement = pos=(0,0,0) rot=(0.57735,0.57735,0.57735;2.0944rad)
  Profile = -> Sketch394
  Ruled = false
  Sections = -> [Sketch395]
FEATURE [Sketcher::SketchObject] Sketch396
  FullyConstrained = true
  MapMode = 5
  Placement = pos=(0,0,0) rot=(0.57735,0.57735,0.57735;2.0944rad)
  Support = -> [YZ_Plane194]
  expr: Constraints[1] = 3 + 2 * <<BaseParameters>>.axisTolerance
  sketch-geometry (1):
    g0: Circle CenterX=0 CenterY=0 CenterZ=0 NormalX=0 NormalY=0 NormalZ=1 AngleXU=0 Radius=1.65
  constraints (2):
    c: Coincident(g0,g-1)
    c: Diameter(g0) = 3.3
FEATURE [PartDesign::Pocket] Pocket158
  BaseFeature = -> AdditiveLoft002
  Direction = (-1,2e-16,-3e-16)
  Length = 19
  Length2 = 5
  Midplane = true
  Placement = pos=(0,0,0) rot=(0.57735,0.57735,0.57735;2.0944rad)
  Profile = -> Sketch396
  ReferenceAxis = -> Sketch396 [N_Axis]
  Type = 0
FEATURE [Sketcher::SketchObject] Sketch397
  FullyConstrained = true
  MapMode = 5
  Support = -> [XY_Plane194]
  expr: Constraints[3] = 3 + 2 * <<BaseParameters>>.axisTolerance
  sketch-geometry (2):
    g0: Circle CenterX=-5 CenterY=0 CenterZ=0 NormalX=0 NormalY=0 NormalZ=1 AngleXU=0 Radius=1.65
    g1: Circle CenterX=5 CenterY=0 CenterZ=0 NormalX=0 NormalY=0 NormalZ=1 AngleXU=0 Radius=1.65
  constraints (5):
    c: PointOnObject(g0,g-1)
    c: Symmetric(g0,g1,g-2)
    c: Distance(g0,g1) = 10
    c: Diameter(g1) = 3.3
    c: Equal(g0,g1)
FEATURE [PartDesign::Pocket] Pocket159
  BaseFeature = -> Pocket158
  Direction = (0,0,-1)
  Length = 10
  Length2 = 5
  Placement = pos=(0,0,0) rot=(0.57735,0.57735,0.57735;2.0944rad)
  Profile = -> Sketch397
  ReferenceAxis = -> Sketch397 [N_Axis]
  Reversed = true
  Type = 0
FEATURE [Sketcher::SketchObject] Sketch398
  FullyConstrained = true
  MapMode = 5
  Placement = pos=(0,0,0) rot=(0.57735,0.57735,0.57735;2.0944rad)
  Support = -> [YZ_Plane194]
  expr: Constraints[11] = 6 + 2 * <<BaseParameters>>.tolerance
  sketch-geometry (5):
    g0: LineSegment StartX=-3.15 StartY=3.15 StartZ=0 EndX=-3.15 EndY=-3.15 EndZ=0
    g1: LineSegment StartX=-3.15 StartY=-3.15 StartZ=0 EndX=3.15 EndY=-3.15 EndZ=0
    g2: LineSegment StartX=3.15 StartY=-3.15 StartZ=0 EndX=3.15 EndY=3.15 EndZ=0
    g3: LineSegment StartX=3.15 StartY=3.15 StartZ=0 EndX=-3.15 EndY=3.15 EndZ=0
    g4: GeomPoint X=-1e-16 Y=1e-16 Z=0
  constraints (12):
    c: Coincident(g0,g1)
    c: Coincident(g1,g2)
    c: Coincident(g2,g3)
    c: Coincident(g3,g0)
    c: Horizontal(g1)
    c: Horizontal(g3)
    c: Vertical(g0)
    c: Vertical(g2)
    c: Symmetric(g1,g0,g4)
    c: Coincident(g4,g-1)
    c: Equal(g3,g2)
    c: Distance(g2) = 6.3
FEATURE [PartDesign::Pocket] Pocket160
  BaseFeature = -> Pocket159
  Direction = (-1,2e-16,-3e-16)
  Length = 6.3
  Length2 = 5
  Midplane = true
  Placement = pos=(0,0,0) rot=(0.57735,0.57735,0.57735;2.0944rad)
  Profile = -> Sketch398
  ReferenceAxis = -> Sketch398 [N_Axis]
  Type = 0
  expr: Length = 6 + 2 * <<BaseParameters>>.tolerance
FEATURE [PartDesign::Body] Body107  label="BaseHinge"
  Group = -> [Sketch393,Pad227,Sketch394,Sketch395,AdditiveLoft002,Sketch396,Pocket158,Sketch397,Pocket159,Sketch398,Pocket160]
  Origin = -> Origin200
  Placement = pos=(0,100,6.15) rot=(-1,0,0;0.17338rad)
  Tip = -> Pocket160
  expr: .Placement.Base.y = <<BaseSkeleton_KeyHolder>>.Constraints.y0
  expr: .Placement.Base.z = <<BaseSkeleton_KeyHolder>>.Constraints.z0
  expr: .Placement.Rotation.Angle = 180deg - <<BaseSkeleton_KeyHolder001>>.Constraints.theta1
FEATURE [Sketcher::SketchObject] Sketch403  label="BaseSkeleton_KeyHolder001"
  FullyConstrained = false
  MapMode = 5
  Placement = pos=(0,0,0) rot=(0.57735,0.57735,0.57735;2.0944rad)
  Support = -> [YZ_Plane106]
  expr: Constraints[18] = <<BaseParameters>>.horizontalRailLength
  expr: Constraints[20] = <<BaseParameters>>.verticalRailLength + 6 + 2 * <<BaseParameters>>.tolerance
  expr: Constraints[24] = <<BaseParameters>>.support0Length
  expr: Constraints[26] = Sketch232.Constraints.l2
  expr: Constraints[27] = Sketch232.Constraints.l3
  expr: Constraints[28] = Sketch232.Constraints.theta1
  expr: Constraints[51] = Sketch232.Constraints.z5
  expr: Constraints[52] = Sketch232.Constraints.y5
  expr: Constraints[59] = Sketch232.Constraints.theta3
  sketch-geometry (16):
    g0: LineSegment StartX=0 StartY=0 StartZ=0 EndX=100 EndY=0 EndZ=0
    g1: LineSegment StartX=100 StartY=0 StartZ=0 EndX=100 EndY=6.15 EndZ=0
    g2: LineSegment StartX=100 StartY=6.15 StartZ=0 EndX=114.888 EndY=91.1561 EndZ=0
    g3: LineSegment StartX=13.6843 StartY=34.7493 StartZ=0 EndX=55.3393 EndY=38.8777 EndZ=0
    g4: LineSegment StartX=55.3393 StartY=38.8777 StartZ=0 EndX=85.053 EndY=63.9051 EndZ=0
    g5: LineSegment StartX=55.3393 StartY=38.8777 StartZ=0 EndX=140.05 EndY=24.0416 EndZ=0
    g6: LineSegment StartX=13.6843 StartY=34.7493 StartZ=0 EndX=22.2563 EndY=6 EndZ=0
    g7: LineSegment StartX=22.2563 StartY=6 StartZ=0 EndX=22.2563 EndY=0 EndZ=0
    g8: GeomPoint X=104.232 Y=30.3146 Z=0
    g9: LineSegment StartX=85.053 StartY=63.9051 StartZ=0 EndX=92.053 EndY=63.9051 EndZ=0
    g10: LineSegment StartX=92.053 StartY=63.9051 StartZ=0 EndX=132.053 EndY=133.187 EndZ=0
    g11: LineSegment StartX=114.888 StartY=91.1561 StartZ=0 EndX=109.562 EndY=94.2311 EndZ=0
    g12: GeomPoint X=100.285 Y=7.77526 Z=0
    g13: LineSegment StartX=85.053 StartY=63.9051 StartZ=0 EndX=109.369 EndY=59.6464 EndZ=0
    g14: LineSegment StartX=15.7537 StartY=34.9544 StartZ=0 EndX=14.7811 EndY=41.5434 EndZ=0
    g15: LineSegment StartX=13.6843 StartY=34.7493 StartZ=0 EndX=13.6843 EndY=39.7493 EndZ=0
  constraints (62):
    c: Coincident(g-1,g0)
    c: PointOnObject(g0,g-1)
    c: Coincident(g0,g1)
    c: Vertical(g1)
    c: Coincident(g1,g2)
    c: Coincident(g3,g4)
    c: Coincident(g3,g5)
    c: Coincident(g3,g6)
    c: Coincident(g6,g7)
    c: PointOnObject(g7,g0)
    c: Vertical(g7)
    c: PointOnObject(g8,g5)
    c: PointOnObject(g8,g2)
    c: Coincident(g4,g9)
    c: Coincident(g9,g10)
    c: Coincident(g11,g2)
    c: PointOnObject(g11,g10)
    c: Perpendicular(g10,g11)
    c: Distance(g0) = 100
    c: Distance(g1) = 6.15
    c: Distance(g2) = 86.3
    c: Distance(g5) = 86
    c: Horizontal(g9)
    c: Distance(g10) = 80
    c: Distance(g6) = 30
    c: Distance(g7) = 6
    c: Distance(g3) = 41.8591
    c: Distance(g4) = 38.8495
    c: Angle(g4,g3) = 2.54038
    c: Distance(g9) = 7
    c: Distance(g11) = 6.15
    c: Perpendicular(g2,g5)
    c: Distance(g7,g-2) = 22.2563  'y0'
    c: Angle(g6,g7) = 2.85182  'theta0'
    c: Angle(g2,g1) = 3.31497  'theta1'
    c: Distance(g8,g-2) = 104.232  'y1'
    c: Distance(g8,g-1) = 30.3146  'z1'
    c: Distance(g3,g8) = 49.637  'l1'
    c: PointOnObject(g12,g2)
    c: Distance(g12,g1) = 1.65
    c: Distance(g2,g-1) = 91.1561  'z2'
    c: Distance(g2,g-2) = 114.888  'y2'
    c: Angle(g10,g2) = 0.350219  'theta2'
    c: Coincident(g13,g4)
    c: PointOnObject(g13,g2)
    c: Perpendicular(g2,g13)
    c: Angle(g10,g9) = 2.0944
    c: Distance(g13) = 24.6863  's2y0'
    c: Distance(g13,g2) = 31.9893  's2z0'
    c: Angle(g13,g9) = 0.17338  's2theta0'
    c: PointOnObject(g14,g3)
    c: Distance(g14) = 6.66044
    c: Distance(g14,g3) = 2.07954
    c: Distance(g14,g-2) = 14.7811  'y3'
    c: Distance(g14,g0) = 41.5434  'z3'
    c: Coincident(g15,g3)
    c: Vertical(g15)
    c: Distance(g15) = 5
    c: Angle(g3,g15) = 1.47201  'theta3'
    c: Angle(g3,g14) = 1.61857
    c: Distance(g12,g-2) = 100.285  'y4'
    c: Distance(g12,g-1) = 7.77526  'z4'
FEATURE [PartDesign::Body] Body064  label="BaseSkeletonHolder"
  Group = -> [Sketch263,Sketch301,Sketch357,Sketch403]
  Origin = -> Origin106
FEATURE [Sketcher::SketchObject] Sketch413
  FullyConstrained = true
  MapMode = 5
  Placement = pos=(0,0,0) rot=(0.57735,0.57735,0.57735;2.0944rad)
  Support = -> [YZ_Plane149]
  expr: Constraints[18] = 1.5 + <<BaseParameters>>.axisTolerance
  sketch-geometry (8):
    g0: LineSegment StartX=0 StartY=1.65 StartZ=0 EndX=0 EndY=3 EndZ=0
    g1: LineSegment StartX=0 StartY=3 StartZ=0 EndX=11 EndY=3 EndZ=0
    g2: ArcOfCircle CenterX=11 CenterY=5 CenterZ=0 NormalX=0 NormalY=0 NormalZ=1 AngleXU=0 Radius=2 StartAngle=4.71239 EndAngle=6.28319
    g3: LineSegment StartX=0 StartY=1.65 StartZ=0 EndX=13 EndY=1.65 EndZ=0
    g4: LineSegment StartX=13 StartY=1.65 StartZ=0 EndX=13 EndY=0 EndZ=0
    g5: LineSegment StartX=13 StartY=0 StartZ=0 EndX=15 EndY=0 EndZ=0
    g6: LineSegment StartX=15 StartY=0 StartZ=0 EndX=15 EndY=5 EndZ=0
    g7: LineSegment StartX=15 StartY=5 StartZ=0 EndX=13 EndY=5 EndZ=0
  constraints (24):
    c: PointOnObject(g0,g-2)
    c: PointOnObject(g0,g-2)
    c: Coincident(g0,g1)
    c: Horizontal(g1)
    c: Tangent(g1,g2) = -1.5708
    c: Coincident(g0,g3)
    c: Horizontal(g3)
    c: Coincident(g3,g4)
    c: PointOnObject(g4,g-1)
    c: Coincident(g4,g5)
    c: PointOnObject(g5,g-1)
    c: Coincident(g5,g6)
    c: Vertical(g6)
    c: Coincident(g6,g7)
    c: Coincident(g7,g2)
    c: Horizontal(g7)
    c: Distance(g7) = 2
    c: Vertical(g4)
    c: Distance(g0,g-1) = 1.65
    c: Distance(g0,g-1) = 3
    c: Distance(g5,g-2) = 15
    c: Vertical(g2,g3)
    c: Perpendicular(g2,g7)
    c: Distance(g6) = 5
FEATURE [PartDesign::Revolution] Revolution001
  Angle = 360
  Axis = (3e-16,1,-2e-16)
  Base = (0,0,0)
  Placement = pos=(0,0,0) rot=(0.57735,0.57735,0.57735;2.0944rad)
  Profile = -> Sketch413
  ReferenceAxis = -> Sketch413 [H_Axis]
FEATURE [PartDesign::Body] Body098  label="SupportHandle"
  Group = -> [Sketch413,Revolution001]
  Origin = -> Origin150
  Placement = pos=(0,126,50) rot=(0,0,1;0rad)
  Tip = -> Revolution001
FEATURE [Sketcher::SketchObject] Sketch418
  FullyConstrained = true
  MapMode = 5
  Support = -> [XY_Plane126]
  sketch-geometry (12):
    g0: LineSegment StartX=10 StartY=0 StartZ=0 EndX=10 EndY=7 EndZ=0
    g1: LineSegment StartX=10 StartY=7 StartZ=0 EndX=22 EndY=7 EndZ=0
    g2: LineSegment StartX=22 StartY=7 StartZ=0 EndX=22 EndY=-3 EndZ=0
    g3: LineSegment StartX=-65 StartY=-3 StartZ=0 EndX=-65 EndY=-23 EndZ=0
    g4: LineSegment StartX=-65 StartY=-23 StartZ=0 EndX=-70 EndY=-23 EndZ=0
    g5: LineSegment StartX=-70 StartY=-23 StartZ=0 EndX=-70 EndY=0 EndZ=0
    g6: LineSegment StartX=-70 StartY=0 StartZ=0 EndX=10 EndY=0 EndZ=0
    g7: LineSegment StartX=22 StartY=-3 StartZ=0 EndX=22 EndY=-23 EndZ=0
    g8: LineSegment StartX=22 StartY=-23 StartZ=0 EndX=17 EndY=-23 EndZ=0
    g9: LineSegment StartX=17 StartY=-23 StartZ=0 EndX=17 EndY=-3 EndZ=0
    g10: LineSegment StartX=22 StartY=-3 StartZ=0 EndX=17 EndY=-3 EndZ=0
    g11: LineSegment StartX=17 StartY=-3 StartZ=0 EndX=-65 EndY=-3 EndZ=0
  constraints (35):
    c: PointOnObject(g0,g-1)
    c: Vertical(g0)
    c: Coincident(g0,g1)
    c: Horizontal(g1)
    c: Coincident(g1,g2)
    c: Vertical(g2)
    c: Coincident(g2,g10)
    c: Coincident(g11,g3)
    c: Vertical(g3)
    c: Coincident(g3,g4)
    c: Horizontal(g4)
    c: Coincident(g4,g5)
    c: PointOnObject(g5,g-1)
    c: Vertical(g5)
    c: Coincident(g5,g6)
    c: Coincident(g6,g0)
    c: Distance(g0,g-2) = 10
    c: Distance(g1) = 12
    c: Distance(g2,g-1) = 3
    c: Distance(g5,g-2) = 70
    c: Distance(g3) = 20
    c: Distance(g4) = 5
    c: Distance(g0) = 7
    c: Coincident(g2,g7)
    c: Vertical(g7)
    c: Coincident(g7,g8)
    c: Horizontal(g8)
    c: Coincident(g8,g9)
    c: Vertical(g9)
    c: Coincident(g10,g11)
    c: Horizontal(g10)
    c: Horizontal(g11)
    c: Coincident(g10,g9)
    c: Equal(g8,g4)
    c: Horizontal(g3,g8)
FEATURE [PartDesign::Pad] Pad233
  Direction = (0,0,1)
  Length = 8
  Length2 = 10
  Midplane = true
  Profile = -> Sketch418
  ReferenceAxis = -> Sketch418 [N_Axis]
  Type = 0
FEATURE [Sketcher::SketchObject] Sketch420
  AttachmentOffset = pos=(0,0,22) rot=(0,0,1;0rad)
  FullyConstrained = true
  MapMode = 5
  Placement = pos=(22,-4.9e-15,4.9e-15) rot=(0.57735,0.57735,0.57735;2.0944rad)
  Support = -> [YZ_Plane126]
  sketch-geometry (4):
    g0: LineSegment StartX=-23 StartY=4 StartZ=0 EndX=-23 EndY=-4 EndZ=0
    g1: LineSegment StartX=-23 StartY=-4 StartZ=0 EndX=-43 EndY=-4 EndZ=0
    g2: LineSegment StartX=-43 StartY=-4 StartZ=0 EndX=-43 EndY=-1 EndZ=0
    g3: LineSegment StartX=-43 StartY=-1 StartZ=0 EndX=-23 EndY=4 EndZ=0
  constraints (11):
    c: Coincident(g0,g1)
    c: Horizontal(g1)
    c: Coincident(g1,g2)
    c: Vertical(g2)
    c: Coincident(g2,g3)
    c: Coincident(g3,g0)
    c: Distance(g2) = 3
    c: Distance(g1) = 20
    c: Distance(g0) = 8
    c: Symmetric(g0,g0,g-1)
    c: Distance(g0,g-2) = 23
FEATURE [PartDesign::Pad] Pad234
  BaseFeature = -> Pad233
  Direction = (1,-2e-16,3e-16)
  Length = 92
  Length2 = 10
  Profile = -> Sketch420
  ReferenceAxis = -> Sketch420 [N_Axis]
  Reversed = true
  Type = 0
FEATURE [Sketcher::SketchObject] Sketch421
  FullyConstrained = true
  MapMode = 5
  Support = -> [XY_Plane126]
  sketch-geometry (3):
    g0: LineSegment StartX=-70 StartY=-33 StartZ=0 EndX=-70 EndY=-43 EndZ=0
    g1: LineSegment StartX=-70 StartY=-43 StartZ=0 EndX=-10 EndY=-43 EndZ=0
    g2: ArcOfCircle CenterX=-70 CenterY=-218 CenterZ=0 NormalX=0 NormalY=0 NormalZ=1 AngleXU=0 Radius=185 StartAngle=1.2405 EndAngle=1.5708
  constraints (10):
    c: Vertical(g0)
    c: Coincident(g0,g1)
    c: Horizontal(g1)
    c: Coincident(g2,g0)
    c: Coincident(g2,g1)
    c: Vertical(g2,g0)
    c: Distance(g0,g-1) = 43
    c: Distance(g0) = 10
    c: Distance(g0,g-2) = 70
    c: Distance(g1,g-2) = 10
FEATURE [PartDesign::Pocket] Pocket172
  BaseFeature = -> Pad234
  Direction = (0,0,-1)
  Length = 13
  Length2 = 5
  Midplane = true
  Profile = -> Sketch421
  ReferenceAxis = -> Sketch421 [N_Axis]
  Type = 0
FEATURE [Sketcher::SketchObject] Sketch422
  AttachmentOffset = pos=(0,0,-24) rot=(0,0,1;0rad)
  FullyConstrained = true
  MapMode = 5
  Placement = pos=(-24,5.3e-15,-5.3e-15) rot=(0.57735,0.57735,0.57735;2.0944rad)
  Support = -> [YZ_Plane126]
  expr: Constraints[1] = 3 + 2 * <<BaseParameters>>.axisTolerance
  sketch-geometry (1):
    g0: Circle CenterX=-13 CenterY=0 CenterZ=0 NormalX=0 NormalY=0 NormalZ=1 AngleXU=0 Radius=1.65
  constraints (3):
    c: PointOnObject(g0,g-1)
    c: Diameter(g0) = 3.3
    c: Distance(g0,g-2) = 13
FEATURE [PartDesign::Pocket] Pocket173
  BaseFeature = -> Pocket172
  Direction = (-1,2e-16,-3e-16)
  Length = 92
  Length2 = 5
  Midplane = true
  Profile = -> Sketch422
  ReferenceAxis = -> Sketch422 [N_Axis]
  Type = 0
FEATURE [Sketcher::SketchObject] Sketch423
  FullyConstrained = true
  MapMode = 5
  Placement = pos=(0,0,0) rot=(1,0,0;1.5708rad)
  Support = -> [XZ_Plane126]
  expr: Constraints[1] = 3 + 2 * <<BaseParameters>>.axisTolerance
  sketch-geometry (1):
    g0: Circle CenterX=16 CenterY=0 CenterZ=0 NormalX=0 NormalY=0 NormalZ=1 AngleXU=0 Radius=1.65
  constraints (3):
    c: PointOnObject(g0,g-1)
    c: Diameter(g0) = 3.3
    c: Distance(g0,g-2) = 16
FEATURE [PartDesign::Pocket] Pocket174
  BaseFeature = -> Pocket173
  Direction = (0,1,2e-16)
  Length = 7
  Length2 = 5
  Profile = -> Sketch423
  ReferenceAxis = -> Sketch423 [N_Axis]
  Type = 0
FEATURE [PartDesign::Body] Body080
  Group = -> [Sketch418,Pad233,Sketch420,Pad234,Sketch421,Pocket172,Sketch422,Pocket173,Sketch423,Pocket174]
  Origin = -> Origin126
  Tip = -> Pocket174
FEATURE [Sketcher::SketchObject] Sketch427
  FullyConstrained = true
  MapMode = 5
  Placement = pos=(0,0,0) rot=(0.57735,0.57735,0.57735;2.0944rad)
  Support = -> [YZ_Plane109]
  sketch-geometry (6):
    g0: LineSegment StartX=3 StartY=-4 StartZ=0 EndX=15 EndY=-4 EndZ=0
    g1: LineSegment StartX=15 StartY=-4 StartZ=0 EndX=15 EndY=7 EndZ=0
    g2: LineSegment StartX=15 StartY=7 StartZ=0 EndX=9 EndY=7 EndZ=0
    g3: LineSegment StartX=3 StartY=-4 StartZ=0 EndX=3 EndY=3 EndZ=0
    g4: ArcOfCircle CenterX=5 CenterY=7 CenterZ=0 NormalX=0 NormalY=0 NormalZ=1 AngleXU=0 Radius=4 StartAngle=4.71239 EndAngle=6.28319
    g5: LineSegment StartX=3 StartY=3 StartZ=0 EndX=5 EndY=3 EndZ=0
  constraints (18):
    c: Horizontal(g0)
    c: Coincident(g0,g1)
    c: Vertical(g1)
    c: Coincident(g1,g2)
    c: Horizontal(g2)
    c: Distance(g0) = 12
    c: Distance(g0,g-2) = 3
    c: Distance(g0,g-1) = 4
    c: Distance(g1,g-1) = 7
    c: Coincident(g0,g3)
    c: Vertical(g3)
    c: Distance(g2) = 6
    c: Coincident(g4,g2)
    c: Coincident(g5,g3)
    c: Horizontal(g5)
    c: Perpendicular(g4,g2)
    c: Tangent(g5,g4) = -1.5708
    c: Distance(g3,g-1) = 3
FEATURE [PartDesign::Pad] Pad235
  BaseFeature = -> Pocket157
  Direction = (1,-2e-16,3e-16)
  Length = 20
  Length2 = 10
  Midplane = true
  Placement = pos=(0,0,0) rot=(0.57735,0.57735,0.57735;2.0944rad)
  Profile = -> Sketch427
  ReferenceAxis = -> Sketch427 [N_Axis]
  Type = 0
FEATURE [Sketcher::SketchObject] Sketch428
  FullyConstrained = true
  MapMode = 5
  Placement = pos=(0,0,0) rot=(0.57735,0.57735,0.57735;2.0944rad)
  Support = -> [YZ_Plane109]
  expr: Constraints[7] = 6 + <<BaseParameters>>.tolerance
  sketch-geometry (6):
    g0: LineSegment StartX=9 StartY=7 StartZ=0 EndX=4.6019 EndY=7 EndZ=0
    g1: ArcOfCircle CenterX=4.6019 CenterY=10 CenterZ=0 NormalX=0 NormalY=0 NormalZ=1 AngleXU=0 Radius=3 StartAngle=3.83826 EndAngle=4.71239
    g2: ArcOfCircle CenterX=0 CenterY=6.15 CenterZ=0 NormalX=0 NormalY=0 NormalZ=1 AngleXU=0 Radius=3 StartAngle=0 EndAngle=0.696669
    g3: LineSegment StartX=3 StartY=6.15 StartZ=0 EndX=3 EndY=3 EndZ=0
    g4: LineSegment StartX=3 StartY=3 StartZ=0 EndX=5 EndY=3 EndZ=0
    g5: ArcOfCircle CenterX=5 CenterY=7 CenterZ=0 NormalX=0 NormalY=0 NormalZ=1 AngleXU=0 Radius=4 StartAngle=4.71239 EndAngle=6.28319
  constraints (17):
    c: Horizontal(g0)
    c: PointOnObject(g2,g-2)
    c: Tangent(g2,g3) = 1.5708
    c: Coincident(g3,g4)
    c: Horizontal(g4)
    c: Coincident(g5,g0)
    c: Vertical(g3)
    c: Distance(g2,g-1) = 6.15
    c: Radius(g2) = 3
    c: Tangent(g2,g1) = 1.5708
    c: Distance(g3,g-1) = 3
    c: Tangent(g5,g4) = -1.5708
    c: Perpendicular(g5,g0)
    c: Distance(g0,g-1) = 7
    c: DistanceX(g3,g0) = 6
    c: Tangent(g1,g0) = 1.5708
    c: Equal(g2,g1)
FEATURE [PartDesign::Pad] Pad236
  BaseFeature = -> Pad235
  Direction = (1,-2e-16,3e-16)
  Length = 6
  Length2 = 10
  Midplane = true
  Placement = pos=(0,0,0) rot=(0.57735,0.57735,0.57735;2.0944rad)
  Profile = -> Sketch428
  ReferenceAxis = -> Sketch428 [N_Axis]
  Type = 0
FEATURE [Sketcher::SketchObject] Sketch429
  AttachmentOffset = pos=(0,0,7) rot=(0,0,1;0rad)
  FullyConstrained = true
  MapMode = 5
  Placement = pos=(0,-7,-1.6e-15) rot=(1,0,0;1.5708rad)
  Support = -> [XZ_Plane109]
  expr: Constraints[1] = 3 + 2 * <<BaseParameters>>.axisTolerance
  sketch-geometry (1):
    g0: Circle CenterX=0 CenterY=0 CenterZ=0 NormalX=0 NormalY=0 NormalZ=1 AngleXU=0 Radius=1.65
  constraints (2):
    c: Coincident(g0,g-1)
    c: Diameter(g0) = 3.3
FEATURE [PartDesign::Pocket] Pocket178
  BaseFeature = -> Pad236
  Direction = (0,1,2e-16)
  Length = 22
  Length2 = 5
  Placement = pos=(0,0,0) rot=(0.57735,0.57735,0.57735;2.0944rad)
  Profile = -> Sketch429
  ReferenceAxis = -> Sketch429 [N_Axis]
  Type = 0
FEATURE [Sketcher::SketchObject] Sketch430
  FullyConstrained = true
  MapMode = 5
  Support = -> [XY_Plane109]
  expr: Constraints[1] = 3 + 2 * <<BaseParameters>>.screwHoleTolerance
  sketch-geometry (1):
    g0: Circle CenterX=0 CenterY=12 CenterZ=0 NormalX=0 NormalY=0 NormalZ=1 AngleXU=0 Radius=1.6
  constraints (3):
    c: PointOnObject(g0,g-2)
    c: Diameter(g0) = 3.2
    c: Distance(g0,g-1) = 12
FEATURE [PartDesign::Pocket] Pocket179
  BaseFeature = -> Pocket178
  Direction = (0,0,-1)
  Length = 7
  Length2 = 5
  Placement = pos=(0,0,0) rot=(0.57735,0.57735,0.57735;2.0944rad)
  Profile = -> Sketch430
  ReferenceAxis = -> Sketch430 [N_Axis]
  Reversed = true
  Type = 0
FEATURE [Sketcher::SketchObject] Sketch431
  AttachmentOffset = pos=(0,0,4) rot=(0,0,1;0rad)
  FullyConstrained = true
  MapMode = 5
  Placement = pos=(0,0,4) rot=(0,0,1;0rad)
  Support = -> [XY_Plane109]
  sketch-geometry (10):
    g0: LineSegment StartX=3.23316 StartY=12 StartZ=0 EndX=1.61658 EndY=14.8 EndZ=0
    g1: LineSegment StartX=1.61658 StartY=14.8 StartZ=0 EndX=-1.61658 EndY=14.8 EndZ=0
    g2: LineSegment StartX=-1.61658 StartY=14.8 StartZ=0 EndX=-3.23316 EndY=12 EndZ=0
    g3: LineSegment StartX=-3.23316 StartY=12 StartZ=0 EndX=-1.61658 EndY=9.2 EndZ=0
    g4: LineSegment StartX=-1.61658 StartY=9.2 StartZ=0 EndX=1.61658 EndY=9.2 EndZ=0
    g5: LineSegment StartX=1.61658 StartY=9.2 StartZ=0 EndX=3.23316 EndY=12 EndZ=0
    g6: Circle CenterX=0 CenterY=12 CenterZ=0 NormalX=0 NormalY=0 NormalZ=1 AngleXU=0 Radius=3.23316
    g7: LineSegment StartX=-3.23316 StartY=12 StartZ=0 EndX=-3.23316 EndY=15 EndZ=0
    g8: LineSegment StartX=-3.23316 StartY=15 StartZ=0 EndX=3.23318 EndY=15 EndZ=0
    g9: LineSegment StartX=3.23318 StartY=15 StartZ=0 EndX=3.23316 EndY=12 EndZ=0
  constraints (25):
    c: Coincident(g0,g1)
    c: Coincident(g1,g2)
    c: Coincident(g2,g3)
    c: Coincident(g3,g4)
    c: Coincident(g4,g5)
    c: Coincident(g5,g0)
    c: Equal(g0, g1-g5) x5
    c: PointOnObject(g0,g6)
    c: PointOnObject(g1,g6)
    c: PointOnObject(g2,g6)
    c: PointOnObject(g3,g6)
    c: PointOnObject(g4,g6)
    c: PointOnObject(g5,g6)
    c: PointOnObject(g6,g-2)
    c: Horizontal(g4)
    c: Distance(g6,g-1) = 12
    c: Distance(g0,g4) = 5.6
    c: Coincident(g2,g7)
    c: Vertical(g7)
    c: Coincident(g7,g8)
    c: Horizontal(g8)
    c: Coincident(g8,g9)
    c: Coincident(g9,g0)
    c: Tangent(g9,g6)
    c: Distance(g9) = 3
FEATURE [PartDesign::Pocket] Pocket180
  BaseFeature = -> Pocket179
  Direction = (0,0,-1)
  Length = 2.6
  Length2 = 5
  Midplane = true
  Placement = pos=(0,0,0) rot=(0.57735,0.57735,0.57735;2.0944rad)
  Profile = -> Sketch431
  ReferenceAxis = -> Sketch431 [N_Axis]
  Type = 0
FEATURE [PartDesign::Body] Body066  label="BaseStructure1"
  Group = -> [Sketch266,Pad170,Sketch269,Pocket087,Sketch392,Pocket157,Sketch427,Pad235,Sketch428,Pad236,Sketch429,Pocket178,Sketch430,Pocket179,Sketch431,Pocket180]
  Origin = -> Origin109
  Placement = pos=(0,100,0) rot=(0,0,1;0rad)
  Tip = -> Pocket180
  expr: .Placement.Base.y = <<BaseSkeleton_KeyHolder>>.Constraints.y0
FEATURE [Sketcher::SketchObject] Sketch432
  AttachmentOffset = pos=(0,0,5) rot=(0,0,1;0rad)
  FullyConstrained = true
  MapMode = 5
  Placement = pos=(5,-1.1e-15,1.1e-15) rot=(0.57735,0.57735,0.57735;2.0944rad)
  Support = -> [YZ_Plane127]
  expr: Constraints[15] = 6 + <<BaseParameters>>.tolerance
  sketch-geometry (6):
    g0: ArcOfCircle CenterX=0 CenterY=6.15 CenterZ=0 NormalX=0 NormalY=0 NormalZ=1 AngleXU=0 Radius=3 StartAngle=6.28318 EndAngle=6.97985
    g1: ArcOfCircle CenterX=4.6019 CenterY=10 CenterZ=0 NormalX=0 NormalY=0 NormalZ=1 AngleXU=0 Radius=3 StartAngle=3.83826 EndAngle=4.71239
    g2: LineSegment StartX=3 StartY=6.14999 StartZ=0 EndX=3 EndY=-4 EndZ=0
    g3: LineSegment StartX=3 StartY=-4 StartZ=0 EndX=15 EndY=-4 EndZ=0
    g4: LineSegment StartX=15 StartY=-4 StartZ=0 EndX=15 EndY=7 EndZ=0
    g5: LineSegment StartX=15 StartY=7 StartZ=0 EndX=4.6019 EndY=7 EndZ=0
  constraints (18):
    c: PointOnObject(g0,g-2)
    c: Coincident(g2,g0)
    c: Vertical(g2)
    c: Coincident(g3,g2)
    c: Horizontal(g3)
    c: Coincident(g4,g3)
    c: Vertical(g4)
    c: Coincident(g5,g4)
    c: Horizontal(g5)
    c: Distance(g2,g-2) = 3
    c: Distance(g2,g-1) = 4
    c: Distance(g3) = 12
    c: Distance(g4,g-1) = 7
    c: Tangent(g5,g1) = 1.5708
    c: Tangent(g1,g0) = 1.5708
    c: Distance(g0,g-1) = 6.15
    c: Radius(g0) = 3
    c: Equal(g0,g1)
FEATURE [PartDesign::Pad] Pad237
  BaseFeature = -> Pad208
  Direction = (1,-2e-16,3e-16)
  Length = 11
  Length2 = 10
  Placement = pos=(0,0,0) rot=(0.57735,0.57735,0.57735;2.0944rad)
  Profile = -> Sketch432
  ReferenceAxis = -> Sketch432 [N_Axis]
  Reversed = true
  Type = 0
FEATURE [PartDesign::Body] Body081
  Group = -> [Sketch306,Pad189,Sketch307,Pocket106,Sketch347,Pad208,Sketch432,Pad237]
  Origin = -> Origin127
  Placement = pos=(16,100,0) rot=(0,0,1;0rad)
  Tip = -> Pad237
  expr: .Placement.Base.y = <<BaseParameters>>.horizontalRailLength
FEATURE [Sketcher::SketchObject] Sketch433
  FullyConstrained = true
  MapMode = 5
  Placement = pos=(0,0,0) rot=(0.57735,0.57735,0.57735;2.0944rad)
  Support = -> [YZ_Plane200]
  sketch-geometry (1):
    g0: Circle CenterX=0 CenterY=0 CenterZ=0 NormalX=0 NormalY=0 NormalZ=1 AngleXU=0 Radius=1.5
  constraints (2):
    c: Coincident(g0,g-1)
    c: Diameter(g0) = 3
FEATURE [PartDesign::Pad] Pad238
  Direction = (1,-2e-16,3e-16)
  Length = 150
  Length2 = 10
  Placement = pos=(0,0,0) rot=(0.57735,0.57735,0.57735;2.0944rad)
  Profile = -> Sketch433
  ReferenceAxis = -> Sketch433 [N_Axis]
  Type = 0
FEATURE [PartDesign::Body] Body112  label="JoystickRail"
  Group = -> [Sketch433,Pad238]
  Origin = -> Origin206
  Placement = pos=(-70,-13,0) rot=(0,0,1;0rad)
  Tip = -> Pad238
COMPONENT P1 — geometry summary ("KeyHolders"; no construction recipe available for this part):
  bounding box: 143.6 x 95.3 x 19.0 mm
  tessellated surface: 36,654 triangles
  volume: 25269 mm^3 (10% of its bounding box)
COMPONENT P2 — geometry summary ("Joystick"; no construction recipe available for this part):
  bounding box: 64.0 x 59.4 x 30.0 mm
  tessellated surface: 48,858 triangles
  volume: 29275 mm^3 (26% of its bounding box)
COMPONENT P3 — recipe-attached ("ThumbKeyHolder", modeled in this document).
Construction recipe (the document's own serialized feature program — sketch geometry with constraints, then the solid features built on it; lengths are millimeters unless a unit is written):

FEATURE [Sketcher::SketchObject] Sketch386
  FullyConstrained = true
  MapMode = 5
  Placement = pos=(0,0,0) rot=(1,0,0;1.5708rad)
  Support = -> [XZ_Plane191]
  expr: Constraints[15] = <<ThumbKeyHolderParameter>>.thumbKeyHolderHeight
  expr: Constraints[16] = Sketch382.Constraints.slotRadius
  sketch-geometry (17):
    g0: LineSegment StartX=-15 StartY=11 StartZ=0 EndX=15 EndY=11 EndZ=0
    g1: LineSegment StartX=20 StartY=-4 StartZ=0 EndX=-15 EndY=-4 EndZ=0
    g2: LineSegment StartX=-15 StartY=-4 StartZ=0 EndX=-15 EndY=11 EndZ=0
    g3: LineSegment StartX=15 StartY=11 StartZ=0 EndX=15 EndY=10 EndZ=0
    g4: ArcOfCircle CenterX=18 CenterY=10 CenterZ=0 NormalX=0 NormalY=0 NormalZ=1 AngleXU=0 Radius=3 StartAngle=3.14159 EndAngle=4.71239
    g5: ArcOfCircle CenterX=0 CenterY=40 CenterZ=0 NormalX=0 NormalY=0 NormalZ=1 AngleXU=0 Radius=38.322 StartAngle=5.24571 EndAngle=8.37758
    g6: ArcOfCircle CenterX=0 CenterY=40 CenterZ=0 NormalX=0 NormalY=0 NormalZ=1 AngleXU=0 Radius=42.322 StartAngle=5.59384 EndAngle=8.37758
    g7: ArcOfCircle CenterX=-20.161 CenterY=74.9199 CenterZ=0 NormalX=0 NormalY=0 NormalZ=1 AngleXU=0 Radius=2 StartAngle=2.0944 EndAngle=5.23599
    g8: LineSegment StartX=0 StartY=40 StartZ=0 EndX=-20.161 EndY=74.9199 EndZ=0
    g9: ArcOfCircle CenterX=35.5268 CenterY=10.7174 CenterZ=0 NormalX=0 NormalY=0 NormalZ=1 AngleXU=0 Radius=3.71737 StartAngle=2.45224 EndAngle=4.71239
    g10: LineSegment StartX=41.5268 StartY=7 StartZ=0 EndX=41.5268 EndY=-4 EndZ=0
    g11: LineSegment StartX=41.5268 StartY=-4 StartZ=0 EndX=20 EndY=-4 EndZ=0
    g12: LineSegment StartX=18 StartY=7 StartZ=0 EndX=19.4828 EndY=7 EndZ=0
    g13: LineSegment StartX=35.5268 StartY=7 StartZ=0 EndX=41.5268 EndY=7 EndZ=0
    g14: GeomPoint X=35.5268 Y=7 Z=0
    g15: GeomPoint X=35.5268 Y=17 Z=0
    g16: GeomPoint X=38.5268 Y=7 Z=0
  constraints (43):
    c: Coincident(g1,g2)
    c: Coincident(g2,g0)
    c: Horizontal(g1)
    c: Vertical(g2)
    c: Distance(g1,g-2) = 15
    c: Distance(g1,g-2) = 20
    c: Distance(g1,g-1) = 4
    c: Distance(g0,g-1) = 11
    c: Coincident(g0,g3)
    c: Vertical(g3)
    c: Symmetric(g0,g0,g-2)
    c: Tangent(g3,g4) = -1.5708
    c: Tangent(g12,g4) = -1.5708
    c: Radius(g4) = 3
    c: PointOnObject(g5,g-2)
    c: Distance(g5,g-1) = 40
    c: Radius(g5) = 38.322
    c: Coincident(g6,g5)
    c: Tangent(g7,g5) = 1.5708
    c: Tangent(g7,g6) = -1.5708
    c: Radius(g7) = 2
    c: Coincident(g8,g5)
    c: Coincident(g8,g7)
    c: Tangent(g9,g6) = 1.5708
    c: Coincident(g13,g10)
    c: Vertical(g10)
    c: Coincident(g10,g11)
    c: Horizontal(g11)
    c: Horizontal(g12)
    c: Coincident(g12,g5)
    c: Distance(g10) = 11
    c: Horizontal(g5,g9)
    c: Horizontal(g13)
    c: Coincident(g11,g1)
    c: Tangent(g9,g13) = -1.5708
    c: Distance(g13) = 6
    c: Coincident(g14,g9)
    c: PointOnObject(g15,g6)
    c: Vertical(g15,g9)
    c: Distance(g15,g9) = 10
    c: Distance(g16,g-2) = 38.5268  'x1'
    c: Symmetric(g9,g10,g16)
    c: Angle(g8,g-2) = 2.61799
FEATURE [PartDesign::Pad] Pad223
  Direction = (0,-1,-2e-16)
  Length = 19
  Length2 = 10
  Midplane = true
  Placement = pos=(0,0,0) rot=(1,0,0;1.5708rad)
  Profile = -> Sketch386
  ReferenceAxis = -> Sketch386 [N_Axis]
  Type = 0
FEATURE [Sketcher::SketchObject] Sketch387
  FullyConstrained = true
  MapMode = 5
  Placement = pos=(0,0,0) rot=(1,0,0;1.5708rad)
  Support = -> [XZ_Plane191]
  expr: Constraints[8] = 3 + <<KeyHolderParameter>>.tolerance
  expr: Constraints[9] = 23 + 2 * <<KeyHolderParameter>>.tolerance
  sketch-geometry (4):
    g0: LineSegment StartX=-11.65 StartY=11 StartZ=0 EndX=11.65 EndY=11 EndZ=0
    g1: LineSegment StartX=11.65 StartY=11 StartZ=0 EndX=11.65 EndY=7.85 EndZ=0
    g2: LineSegment StartX=11.65 StartY=7.85 StartZ=0 EndX=-11.65 EndY=7.85 EndZ=0
    g3: LineSegment StartX=-11.65 StartY=7.85 StartZ=0 EndX=-11.65 EndY=11 EndZ=0
  constraints (11):
    c: Coincident(g0,g1)
    c: Coincident(g1,g2)
    c: Coincident(g2,g3)
    c: Coincident(g3,g0)
    c: Horizontal(g2)
    c: Vertical(g1)
    c: Vertical(g3)
    c: Symmetric(g0,g0,g-2)
    c: Distance(g3) = 3.15
    c: Distance(g0) = 23.3
    c: Distance(g0,g-1) = 11
FEATURE [PartDesign::Pocket] Pocket155
  BaseFeature = -> Pad223
  Direction = (0,1,2e-16)
  Length = 19
  Length2 = 5
  Midplane = true
  Placement = pos=(0,0,0) rot=(1,0,0;1.5708rad)
  Profile = -> Sketch387
  ReferenceAxis = -> Sketch387 [N_Axis]
  Type = 0
FEATURE [Sketcher::SketchObject] Sketch388
  FullyConstrained = true
  MapMode = 5
  Placement = pos=(0,0,0) rot=(1,0,0;1.5708rad)
  Support = -> [XZ_Plane191]
  expr: Constraints[7] = 23 + 2 * <<KeyHolderParameter>>.tolerance
  sketch-geometry (4):
    g0: LineSegment StartX=-11.65 StartY=11 StartZ=0 EndX=11.65 EndY=11 EndZ=0
    g1: LineSegment StartX=11.65 StartY=11 StartZ=0 EndX=11.65 EndY=-4 EndZ=0
    g2: LineSegment StartX=11.65 StartY=-4 StartZ=0 EndX=-11.65 EndY=-4 EndZ=0
    g3: LineSegment StartX=-11.65 StartY=-4 StartZ=0 EndX=-11.65 EndY=11 EndZ=0
  constraints (11):
    c: Coincident(g0,g1)
    c: Coincident(g1,g2)
    c: Coincident(g2,g3)
    c: Coincident(g3,g0)
    c: Horizontal(g2)
    c: Vertical(g1)
    c: Vertical(g3)
    c: Distance(g0) = 23.3
    c: Symmetric(g0,g0,g-2)
    c: Distance(g0,g-1) = 11
    c: Distance(g3) = 15
FEATURE [PartDesign::Pocket] Pocket156
  BaseFeature = -> Pocket155
  Direction = (0,1,2e-16)
  Length = 15
  Length2 = 5
  Midplane = true
  Placement = pos=(0,0,0) rot=(1,0,0;1.5708rad)
  Profile = -> Sketch388
  ReferenceAxis = -> Sketch388 [N_Axis]
  Type = 0
FEATURE [Sketcher::SketchObject] Sketch435
  AttachmentOffset = pos=(0,0,-15) rot=(0,0,1;0rad)
  FullyConstrained = true
  MapMode = 5
  Placement = pos=(-15,3.3e-15,-3.3e-15) rot=(0.57735,0.57735,0.57735;2.0944rad)
  Support = -> [YZ_Plane191]
  expr: Constraints[1] = 3 + 2 * <<BaseParameters>>.axisTolerance
  sketch-geometry (1):
    g0: Circle CenterX=0 CenterY=0 CenterZ=0 NormalX=0 NormalY=0 NormalZ=1 AngleXU=0 Radius=1.65
  constraints (2):
    c: Coincident(g0,g-1)
    c: Diameter(g0) = 3.3
FEATURE [PartDesign::Pocket] Pocket182
  BaseFeature = -> Pocket156
  Direction = (-1,2e-16,-3e-16)
  Length = 58
  Length2 = 5
  Placement = pos=(0,0,0) rot=(1,0,0;1.5708rad)
  Profile = -> Sketch435
  ReferenceAxis = -> Sketch435 [N_Axis]
  Reversed = true
  Type = 0
FEATURE [Sketcher::SketchObject] Sketch436
  AttachmentOffset = pos=(0,0,4) rot=(0,0,1;0rad)
  FullyConstrained = true
  MapMode = 5
  Placement = pos=(0,0,4) rot=(0,0,1;0rad)
  Support = -> [XY_Plane191]
  expr: Constraints[18] = Sketch386.Constraints.x1
  sketch-geometry (10):
    g0: LineSegment StartX=38.5268 StartY=-3.23316 StartZ=0 EndX=41.3268 EndY=-1.61658 EndZ=0
    g1: LineSegment StartX=41.3268 StartY=-1.61658 StartZ=0 EndX=41.3268 EndY=1.61658 EndZ=0
    g2: LineSegment StartX=41.3268 StartY=1.61658 StartZ=0 EndX=38.5268 EndY=3.23316 EndZ=0
    g3: LineSegment StartX=38.5268 StartY=3.23316 StartZ=0 EndX=35.7268 EndY=1.61658 EndZ=0
    g4: LineSegment StartX=35.7268 StartY=1.61658 StartZ=0 EndX=35.7268 EndY=-1.61658 EndZ=0
    g5: LineSegment StartX=35.7268 StartY=-1.61658 StartZ=0 EndX=38.5268 EndY=-3.23316 EndZ=0
    g6: Circle CenterX=38.5268 CenterY=0 CenterZ=0 NormalX=0 NormalY=0 NormalZ=1 AngleXU=0 Radius=3.23316
    g7: LineSegment StartX=38.5268 StartY=3.23316 StartZ=0 EndX=41.76 EndY=3.23316 EndZ=0
    g8: LineSegment StartX=41.76 StartY=3.23316 StartZ=0 EndX=41.76 EndY=-3.23318 EndZ=0
    g9: LineSegment StartX=41.76 StartY=-3.23318 StartZ=0 EndX=38.5268 EndY=-3.23316 EndZ=0
  constraints (25):
    c: Coincident(g0,g1)
    c: Coincident(g1,g2)
    c: Coincident(g2,g3)
    c: Coincident(g3,g4)
    c: Coincident(g4,g5)
    c: Coincident(g5,g0)
    c: Equal(g0, g1-g5) x5
    c: PointOnObject(g0,g6)
    c: PointOnObject(g1,g6)
    c: PointOnObject(g2,g6)
    c: PointOnObject(g3,g6)
    c: PointOnObject(g4,g6)
    c: PointOnObject(g5,g6)
    c: PointOnObject(g6,g-1)
    c: Distance(g6,g-2) = 38.5268
    c: Distance(g3,g1) = 5.6
    c: Vertical(g1)
    c: Coincident(g2,g7)
    c: Horizontal(g7)
    c: Coincident(g7,g8)
    c: Vertical(g8)
    c: Tangent(g8,g6)
    c: Coincident(g8,g9)
    c: Coincident(g9,g0)
    c: Tangent(g9,g6)
FEATURE [PartDesign::Pocket] Pocket183
  BaseFeature = -> Pocket182
  Direction = (0,0,-1)
  Length = 2.6
  Length2 = 5
  Midplane = true
  Placement = pos=(0,0,0) rot=(1,0,0;1.5708rad)
  Profile = -> Sketch436
  ReferenceAxis = -> Sketch436 [N_Axis]
  Type = 0
FEATURE [Sketcher::SketchObject] Sketch437
  FullyConstrained = true
  MapMode = 5
  Support = -> [XY_Plane191]
  expr: Constraints[1] = 3 + 2 * <<BaseParameters>>.screwHoleTolerance
  expr: Constraints[2] = Sketch386.Constraints.x1
  sketch-geometry (1):
    g0: Circle CenterX=38.5268 CenterY=0 CenterZ=0 NormalX=0 NormalY=0 NormalZ=1 AngleXU=0 Radius=1.6
  constraints (3):
    c: PointOnObject(g0,g-1)
    c: Diameter(g0) = 3.2
    c: Distance(g0,g-2) = 38.5268
FEATURE [PartDesign::Pocket] Pocket184
  BaseFeature = -> Pocket183
  Direction = (0,0,-1)
  Length = 12
  Length2 = 5
  Placement = pos=(0,0,0) rot=(1,0,0;1.5708rad)
  Profile = -> Sketch437
  ReferenceAxis = -> Sketch437 [N_Axis]
  Reversed = true
  Type = 0
FEATURE [PartDesign::Body] Body105  label="ThumbKeyHolderStator"
  Group = -> [Sketch386,Pad223,Sketch387,Pocket155,Sketch388,Pocket156,Sketch435,Pocket182,Sketch436,Pocket183,Sketch437,Pocket184]
  Origin = -> Origin196
  Tip = -> Pocket184
COMPONENT P4 — recipe-attached ("KeyHolderFrameAforRingAndLittle", modeled in this document).
Construction recipe (the document's own serialized feature program — sketch geometry with constraints, then the solid features built on it; lengths are millimeters unless a unit is written):

FEATURE [PartDesign::Pad] Pad207
  Direction = (1,-2e-16,3e-16)
  Length = 19
  Length2 = 10
  Midplane = true
  Placement = pos=(0,0,0) rot=(0.57735,0.57735,0.57735;2.0944rad)
  Profile = -> Sketch203
  ReferenceAxis = -> Sketch203 [N_Axis]
  Type = 0
FEATURE [PartDesign::Pocket] Pocket131
  BaseFeature = -> Pad207
  Direction = (-1,2e-16,-3e-16)
  Length = 19
  Length2 = 5
  Midplane = true
  Placement = pos=(0,0,0) rot=(0.57735,0.57735,0.57735;2.0944rad)
  Profile = -> Sketch204
  ReferenceAxis = -> Sketch204 [N_Axis]
  Type = 0
FEATURE [PartDesign::Pocket] Pocket130
  BaseFeature = -> Pocket131
  Direction = (-1,2e-16,-3e-16)
  Length = 15
  Length2 = 5
  Midplane = true
  Placement = pos=(0,0,0) rot=(0.57735,0.57735,0.57735;2.0944rad)
  Profile = -> Sketch205
  ReferenceAxis = -> Sketch205 [N_Axis]
  Type = 0
FEATURE [PartDesign::Pocket] Pocket133
  BaseFeature = -> Pocket130
  Direction = (-1,2e-16,-3e-16)
  Length = 10.3
  Length2 = 5
  Midplane = true
  Placement = pos=(0,0,0) rot=(0.57735,0.57735,0.57735;2.0944rad)
  Profile = -> Sketch233
  ReferenceAxis = -> Sketch233 [N_Axis]
  Type = 0
  expr: Length = 10 + <<KeyHolderParameter>>.tolerance * 2
FEATURE [PartDesign::Body] Body097  label="Ring"
  Group = -> [Pad207,Pocket131,Pocket130,Pocket133]
  Origin = -> Origin149
  Tip = -> Pocket133
FEATURE [PartDesign::Pad] Pad222
  Direction = (1,-2e-16,3e-16)
  Length = 19
  Length2 = 10
  Midplane = true
  Placement = pos=(0,0,0) rot=(0.57735,0.57735,0.57735;2.0944rad)
  Profile = -> Sketch203
  ReferenceAxis = -> Sketch203 [N_Axis]
  Type = 0
FEATURE [PartDesign::Pocket] Pocket152
  BaseFeature = -> Pad222
  Direction = (-1,2e-16,-3e-16)
  Length = 19
  Length2 = 5
  Midplane = true
  Placement = pos=(0,0,0) rot=(0.57735,0.57735,0.57735;2.0944rad)
  Profile = -> Sketch204
  ReferenceAxis = -> Sketch204 [N_Axis]
  Type = 0
FEATURE [PartDesign::Pocket] Pocket150
  BaseFeature = -> Pocket152
  Direction = (-1,2e-16,-3e-16)
  Length = 15
  Length2 = 5
  Midplane = true
  Placement = pos=(0,0,0) rot=(0.57735,0.57735,0.57735;2.0944rad)
  Profile = -> Sketch205
  ReferenceAxis = -> Sketch205 [N_Axis]
  Type = 0
FEATURE [PartDesign::Pocket] Pocket151
  BaseFeature = -> Pocket150
  Direction = (-1,2e-16,-3e-16)
  Length = 10.3
  Length2 = 5
  Midplane = true
  Placement = pos=(0,0,0) rot=(0.57735,0.57735,0.57735;2.0944rad)
  Profile = -> Sketch233
  ReferenceAxis = -> Sketch233 [N_Axis]
  Type = 0
  expr: Length = 10 + <<KeyHolderParameter>>.tolerance * 2
FEATURE [Sketcher::SketchObject] Sketch384
  FullyConstrained = true
  MapMode = 5
  Placement = pos=(0,0,0) rot=(0.57735,0.57735,0.57735;2.0944rad)
  Support = -> [YZ_Plane084]
  expr: Constraints[0] = Sketch203.Constraints.y3
  expr: Constraints[1] = Sketch203.Constraints.z3
  expr: Constraints[8] = <<KeyHolderParameter>>.key3theta
  sketch-geometry (8):
    g0: GeomPoint X=57.0892 Y=14.825 Z=0
    g1: LineSegment StartX=57.0892 StartY=14.825 StartZ=0 EndX=68.5892 EndY=21.4645 EndZ=0
    g2: LineSegment StartX=70.0892 StartY=24.0626 StartZ=0 EndX=70.0892 EndY=42.3306 EndZ=0
    g3: LineSegment StartX=70.0892 StartY=42.3306 StartZ=0 EndX=56.2494 EndY=66.3017 EndZ=0
    g4: LineSegment StartX=56.2494 StartY=66.3017 StartZ=0 EndX=34.5892 EndY=53.7961 EndZ=0
    g5: LineSegment StartX=34.5892 StartY=53.7961 StartZ=0 EndX=57.0892 EndY=14.825 EndZ=0
    g6: ArcOfCircle CenterX=67.0892 CenterY=24.0626 CenterZ=0 NormalX=0 NormalY=0 NormalZ=1 AngleXU=0 Radius=3 StartAngle=5.23599 EndAngle=6.28319
    g7: GeomPoint X=70.0892 Y=22.3306 Z=0
  constraints (20):
    c: Distance(g0,g-2) = 57.0892
    c: Distance(g0,g-1) = 14.825
    c: Coincident(g1,g0)
    c: Vertical(g2)
    c: Coincident(g2,g3)
    c: Coincident(g3,g4)
    c: Coincident(g4,g5)
    c: Coincident(g5,g1)
    c: Angle(g1,g-1) = 2.61799
    c: DistanceX(g1,g7) = 13
    c: Perpendicular(g1,g5)
    c: Parallel(g5,g3)
    c: Parallel(g4,g1)
    c: Distance(g2,g7) = 20
    c: Distance(g5) = 45
    c: PointOnObject(g7,g1)
    c: PointOnObject(g7,g2)
    c: Tangent(g1,g6) = -1.5708
    c: Tangent(g2,g6) = -1.5708
    c: Radius(g6) = 3
FEATURE [PartDesign::Pocket] Pocket153
  BaseFeature = -> Pocket151
  Direction = (-1,2e-16,-3e-16)
  Length = 20
  Length2 = 5
  Midplane = true
  Placement = pos=(0,0,0) rot=(0.57735,0.57735,0.57735;2.0944rad)
  Profile = -> Sketch384
  ReferenceAxis = -> Sketch384 [N_Axis]
  Type = 0
FEATURE [PartDesign::Body] Body104  label="Little"
  Group = -> [Pad222,Pocket152,Pocket150,Pocket151,Sketch384,Pocket153]
  Origin = -> Origin193
  Placement = pos=(-20,0,0) rot=(0,0,1;0rad)
  Tip = -> Pocket153
COMPONENT P5 — recipe-attached ("Miscellaneous", modeled in this document).
Construction recipe (the document's own serialized feature program — sketch geometry with constraints, then the solid features built on it; lengths are millimeters unless a unit is written):

FEATURE [Sketcher::SketchObject] Sketch410
  FullyConstrained = true
  MapMode = 5
  Placement = pos=(0,0,0) rot=(0.57735,0.57735,0.57735;2.0944rad)
  Support = -> [YZ_Plane196]
  sketch-geometry (6):
    g0: LineSegment StartX=0 StartY=0 StartZ=0 EndX=0 EndY=2.75 EndZ=0
    g1: LineSegment StartX=0 StartY=2.75 StartZ=0 EndX=3 EndY=2.75 EndZ=0
    g2: LineSegment StartX=3 StartY=2.75 StartZ=0 EndX=3 EndY=5 EndZ=0
    g3: LineSegment StartX=3 StartY=5 StartZ=0 EndX=-5 EndY=5 EndZ=0
    g4: LineSegment StartX=-5 StartY=5 StartZ=0 EndX=-5 EndY=0 EndZ=0
    g5: LineSegment StartX=-5 StartY=0 StartZ=0 EndX=0 EndY=0 EndZ=0
  constraints (17):
    c: Coincident(g-1,g0)
    c: PointOnObject(g0,g-2)
    c: Coincident(g0,g1)
    c: Coincident(g1,g2)
    c: Vertical(g2)
    c: Coincident(g2,g3)
    c: Horizontal(g3)
    c: Coincident(g3,g4)
    c: PointOnObject(g4,g-1)
    c: Vertical(g4)
    c: Coincident(g4,g5)
    c: Coincident(g5,g0)
    c: Horizontal(g1)
    c: Distance(g1) = 3
    c: Distance(g1,g-1) = 2.75
    c: Distance(g2,g-1) = 5
    c: Distance(g3) = 8
FEATURE [PartDesign::Revolution] Revolution
  Angle = 360
  Axis = (3e-16,1,-2e-16)
  Base = (0,0,0)
  Placement = pos=(0,0,0) rot=(0.57735,0.57735,0.57735;2.0944rad)
  Profile = -> Sketch410
  ReferenceAxis = -> Sketch410 [H_Axis]
FEATURE [Sketcher::SketchObject] Sketch411
  FullyConstrained = true
  MapMode = 5
  Placement = pos=(0,0,0) rot=(1,0,0;1.5708rad)
  Support = -> [XZ_Plane196]
  sketch-geometry (4):
    g0: LineSegment StartX=-0.415571 StartY=-4.75 StartZ=0 EndX=0.415571 EndY=-4.75 EndZ=0
    g1: LineSegment StartX=0.415571 StartY=-4.75 StartZ=0 EndX=0.437443 EndY=-5 EndZ=0
    g2: LineSegment StartX=0.437443 StartY=-5 StartZ=0 EndX=-0.437443 EndY=-5 EndZ=0
    g3: LineSegment StartX=-0.437443 StartY=-5 StartZ=0 EndX=-0.415571 EndY=-4.75 EndZ=0
  constraints (11):
    c: Coincident(g0,g1)
    c: Coincident(g1,g2)
    c: Coincident(g2,g3)
    c: Coincident(g3,g0)
    c: Horizontal(g2)
    c: Symmetric(g0,g0,g-2)
    c: Distance(g1,g-1) = 5
    c: PointOnObject(g-1,g3)
    c: PointOnObject(g-1,g1)
    c: Angle(g3,g1) = 0.174533
    c: Distance(g0,g2) = 0.25
FEATURE [PartDesign::Pocket] Pocket170
  BaseFeature = -> Revolution
  Direction = (0,1,-2e-16)
  Length = 10
  Length2 = 5
  Midplane = true
  Placement = pos=(0,0,0) rot=(0.57735,0.57735,0.57735;2.0944rad)
  Profile = -> Sketch411
  ReferenceAxis = -> Sketch411 [N_Axis]
  Type = 0
FEATURE [PartDesign::PolarPattern] PolarPattern
  Angle = 360
  Axis = -> Sketch411 [N_Axis]
  BaseFeature = -> Pocket170
  Occurrences = 18
  Originals = -> [Pocket170]
  Placement = pos=(0,0,0) rot=(0.57735,0.57735,0.57735;2.0944rad)
FEATURE [Sketcher::SketchObject] Sketch412
  FullyConstrained = true
  MapMode = 5
  Placement = pos=(0,0,0) rot=(1,0,0;1.5708rad)
  Support = -> [XZ_Plane196]
  sketch-geometry (7):
    g0: LineSegment StartX=2.4218e-12 StartY=-1.44338 StartZ=0 EndX=1.25 EndY=-0.721688 EndZ=0
    g1: LineSegment StartX=1.25 StartY=-0.721688 StartZ=0 EndX=1.25 EndY=0.721688 EndZ=0
    g2: LineSegment StartX=1.25 StartY=0.721688 StartZ=0 EndX=-9.064e-13 EndY=1.44338 EndZ=0
    g3: LineSegment StartX=-9.065e-13 StartY=1.44338 StartZ=0 EndX=-1.25 EndY=0.721688 EndZ=0
    g4: LineSegment StartX=-1.25 StartY=0.721688 StartZ=0 EndX=-1.25 EndY=-0.721688 EndZ=0
    g5: LineSegment StartX=-1.25 StartY=-0.721688 StartZ=0 EndX=2.4218e-12 EndY=-1.44338 EndZ=0
    g6: Circle CenterX=0 CenterY=0 CenterZ=0 NormalX=0 NormalY=0 NormalZ=1 AngleXU=0 Radius=1.44338
  constraints (16):
    c: Coincident(g0,g1)
    c: Coincident(g1,g2)
    c: Coincident(g2,g3)
    c: Coincident(g3,g4)
    c: Coincident(g4,g5)
    c: Coincident(g5,g0)
    c: Equal(g0, g1-g5) x5
    c: PointOnObject(g0,g6)
    c: PointOnObject(g1,g6)
    c: PointOnObject(g2,g6)
    c: PointOnObject(g3,g6)
    c: PointOnObject(g4,g6)
    c: PointOnObject(g5,g6)
    c: Coincident(g6,g-1)
    c: Vertical(g1)
    c: Distance(g3,g1) = 2.5
FEATURE [PartDesign::Pad] Pad229
  BaseFeature = -> PolarPattern
  Direction = (0,-1,2e-16)
  Length = 1.5
  Length2 = 10
  Placement = pos=(0,0,0) rot=(0.57735,0.57735,0.57735;2.0944rad)
  Profile = -> Sketch412
  ReferenceAxis = -> Sketch412 [N_Axis]
  Reversed = true
  Type = 0
FEATURE [PartDesign::Body] Body109  label="ScrewCap"
  Group = -> [Sketch410,Revolution,Sketch411,Pocket170,PolarPattern,Sketch412,Pad229]
  Origin = -> Origin202
  Tip = -> Pad229
FEATURE [Sketcher::SketchObject] Sketch414
  FullyConstrained = true
  MapMode = 5
  Support = -> [XY_Plane198]
  sketch-geometry (1):
    g0: Circle CenterX=0 CenterY=0 CenterZ=0 NormalX=0 NormalY=0 NormalZ=1 AngleXU=0 Radius=1.5
  constraints (2):
    c: Coincident(g0,g-1)
    c: Diameter(g0) = 3
FEATURE [PartDesign::Pad] Pad230
  Direction = (0,0,1)
  Length = 11
  Length2 = 10
  Profile = -> Sketch414
  ReferenceAxis = -> Sketch414 [N_Axis]
  Type = 0
FEATURE [Sketcher::SketchObject] Sketch415
  FullyConstrained = true
  MapMode = 5
  Support = -> [XY_Plane198]
  sketch-geometry (1):
    g0: Circle CenterX=0 CenterY=0 CenterZ=0 NormalX=0 NormalY=0 NormalZ=1 AngleXU=0 Radius=2.5
  constraints (2):
    c: Coincident(g0,g-1)
    c: Diameter(g0) = 5
FEATURE [PartDesign::Pad] Pad231
  BaseFeature = -> Pad230
  Direction = (0,0,1)
  Length = 2
  Length2 = 10
  Profile = -> Sketch415
  ReferenceAxis = -> Sketch415 [N_Axis]
  Reversed = true
  Type = 0
FEATURE [PartDesign::Body] Body110  label="PrintableAxis"
  Group = -> [Sketch414,Pad230,Sketch415,Pad231]
  Origin = -> Origin204
  Placement = pos=(-15.1,0,0) rot=(0,0,1;0rad)
  Tip = -> Pad231
PROVENANCE & LICENSES
A FreeCAD (.FCStd) document from a public repository crawl; recipes are the document's own serialized feature recipes (and, for linked parts, companion documents' recipes).
License: mit.
